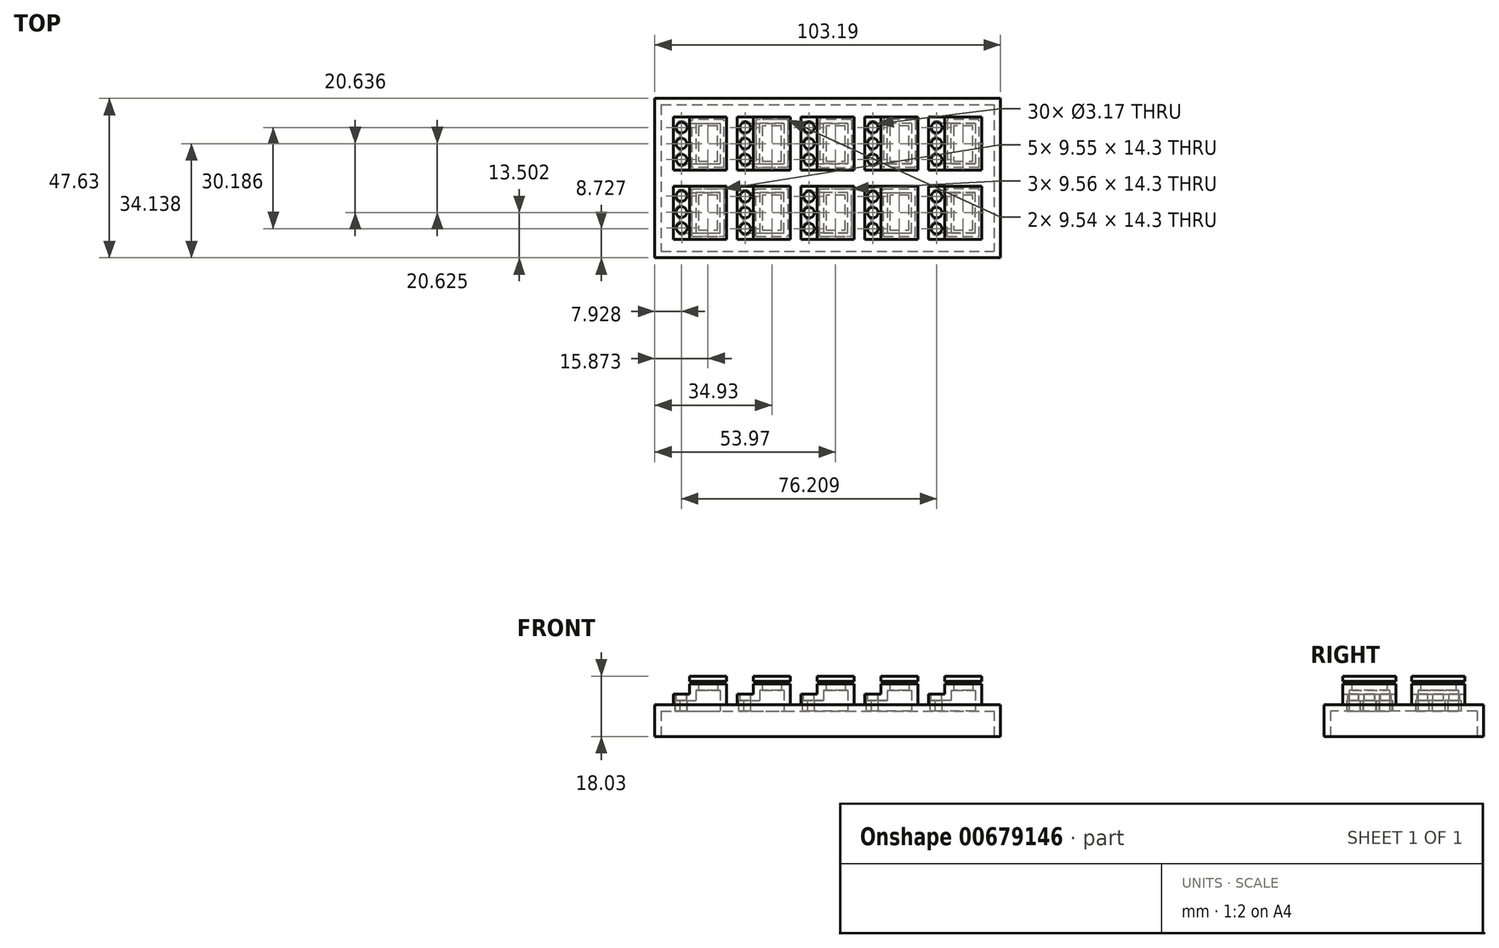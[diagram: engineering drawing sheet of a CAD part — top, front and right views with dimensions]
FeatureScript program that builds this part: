
annotation { "Feature Type Name" : "Feature", "Feature Type Description" : "" }
export const myFeature = defineFeature(function(context is Context, id is Id, definition is map)
    precondition{}
    {
        {
            var Q0;
            Q0=qCreatedBy(makeId("Top.planeOp"),FACE);
            var sketch = newSketch(context, id + "F0", { "sketchPlane" : qUnion([Q0])});
            skLineSegment(sketch, "E0.bottom", {"start": v(-47.56, -3.6) * mm, "end": v(55.63, -3.6) * mm});
            skLineSegment(sketch, "E0.top", {"start": v(-47.56, -51.22) * mm, "end": v(55.63, -51.22) * mm});
            skLineSegment(sketch, "E0.left", {"start": v(-47.56, -3.6) * mm, "end": v(-47.56, -51.22) * mm});
            skLineSegment(sketch, "E0.right", {"start": v(55.63, -3.6) * mm, "end": v(55.63, -51.22) * mm});
            skSolve(sketch);
        }
        {
            var Q0;
            Q0=makeQuery(id+"F0.imprint","IMPRINT",FACE,{"disambiguationData":[TD([[makeQuery(id+"F0.imprint","IMPRINT",EDGE,{"derivedFrom":sQuery(id+"F0.wireOp",EDGE,"E0.bottom")}),-1.0]])]});
            extrude(context, id + "F1", {"entities" : qUnion([Q0]), "depth" : 9.52 * mm, "offsetDistance" : 25.4 * mm});
        }
        {
            var Q0;
            Q0=makeQuery(id+"F1.opExtrude","CAP_FACE",FACE,{"disambiguationData":[OSD([sQuery(id+"F0.wireOp",EDGE,"E0.bottom"),sQuery(id+"F0.wireOp",EDGE,"E0.top"),sQuery(id+"F0.wireOp",EDGE,"E0.left"),sQuery(id+"F0.wireOp",EDGE,"E0.right")])],"isStart":false});
            var sketch = newSketch(context, id + "F2", { "sketchPlane" : qUnion([Q0])});
            skLineSegment(sketch, "E1.bottom", {"start": v(-42, -45.66) * mm, "end": v(-26.12, -45.66) * mm});
            skLineSegment(sketch, "E1.top", {"start": v(-42, -29.78) * mm, "end": v(-26.12, -29.78) * mm});
            skLineSegment(sketch, "E1.left", {"start": v(-42, -45.66) * mm, "end": v(-42, -29.78) * mm});
            skLineSegment(sketch, "E1.right", {"start": v(-26.12, -45.66) * mm, "end": v(-26.12, -29.78) * mm});
            skLineSegment(sketch, "E2.bottom", {"start": v(-42, -9.16) * mm, "end": v(-26.12, -9.16) * mm});
            skLineSegment(sketch, "E2.top", {"start": v(-42, -25.03) * mm, "end": v(-26.12, -25.03) * mm});
            skLineSegment(sketch, "E2.left", {"start": v(-42, -9.16) * mm, "end": v(-42, -25.03) * mm});
            skLineSegment(sketch, "E2.right", {"start": v(-26.12, -9.16) * mm, "end": v(-26.12, -25.03) * mm});
            skLineSegment(sketch, "E3.bottom", {"start": v(50.08, -45.66) * mm, "end": v(34.2, -45.66) * mm});
            skLineSegment(sketch, "E3.top", {"start": v(50.08, -29.78) * mm, "end": v(34.2, -29.78) * mm});
            skLineSegment(sketch, "E3.left", {"start": v(50.08, -45.66) * mm, "end": v(50.08, -29.78) * mm});
            skLineSegment(sketch, "E3.right", {"start": v(34.2, -45.66) * mm, "end": v(34.2, -29.78) * mm});
            skLineSegment(sketch, "E4.bottom", {"start": v(50.08, -9.16) * mm, "end": v(34.2, -9.16) * mm});
            skLineSegment(sketch, "E4.top", {"start": v(50.08, -25.03) * mm, "end": v(34.2, -25.03) * mm});
            skLineSegment(sketch, "E4.left", {"start": v(50.08, -9.16) * mm, "end": v(50.08, -25.03) * mm});
            skLineSegment(sketch, "E4.right", {"start": v(34.2, -9.16) * mm, "end": v(34.2, -25.03) * mm});
            skLineSegment(sketch, "E5.bottom", {"start": v(-22.95, -9.14) * mm, "end": v(-7.07, -9.14) * mm});
            skLineSegment(sketch, "E5.top", {"start": v(-22.95, -25.02) * mm, "end": v(-7.07, -25.02) * mm});
            skLineSegment(sketch, "E5.left", {"start": v(-22.95, -9.14) * mm, "end": v(-22.95, -25.02) * mm});
            skLineSegment(sketch, "E5.right", {"start": v(-7.07, -9.14) * mm, "end": v(-7.07, -25.02) * mm});
            skLineSegment(sketch, "E6.bottom", {"start": v(-22.95, -45.66) * mm, "end": v(-7.07, -45.66) * mm});
            skLineSegment(sketch, "E6.top", {"start": v(-22.95, -29.78) * mm, "end": v(-7.07, -29.78) * mm});
            skLineSegment(sketch, "E6.left", {"start": v(-22.95, -45.66) * mm, "end": v(-22.95, -29.78) * mm});
            skLineSegment(sketch, "E6.right", {"start": v(-7.07, -45.66) * mm, "end": v(-7.07, -29.78) * mm});
            skLineSegment(sketch, "E7.right", {"start": v(15.15, -9.14) * mm, "end": v(15.15, -25.02) * mm});
            skLineSegment(sketch, "E8.right", {"start": v(15.15, -45.66) * mm, "end": v(15.15, -29.78) * mm});
            skLineSegment(sketch, "E9.bottom", {"start": v(12.03, -45.66) * mm, "end": v(31.03, -45.66) * mm});
            skLineSegment(sketch, "E9.top", {"start": v(12.03, -29.78) * mm, "end": v(31.03, -29.78) * mm});
            skLineSegment(sketch, "E9.right", {"start": v(31.03, -45.66) * mm, "end": v(31.03, -29.78) * mm});
            skLineSegment(sketch, "E10.bottom", {"start": v(31.03, -9.14) * mm, "end": v(12.03, -9.14) * mm});
            skLineSegment(sketch, "E10.top", {"start": v(31.03, -25.02) * mm, "end": v(12.03, -25.02) * mm});
            skLineSegment(sketch, "E10.left", {"start": v(31.03, -9.14) * mm, "end": v(31.03, -25.02) * mm});
            skLineSegment(sketch, "E11.bottom", {"start": v(11.98, -45.66) * mm, "end": v(-3.9, -45.66) * mm});
            skLineSegment(sketch, "E11.top", {"start": v(11.98, -29.78) * mm, "end": v(-3.9, -29.78) * mm});
            skLineSegment(sketch, "E11.left", {"start": v(11.98, -45.66) * mm, "end": v(11.98, -29.78) * mm});
            skLineSegment(sketch, "E11.right", {"start": v(-3.9, -45.66) * mm, "end": v(-3.9, -29.78) * mm});
            skLineSegment(sketch, "E12.bottom", {"start": v(-3.9, -9.14) * mm, "end": v(11.98, -9.14) * mm});
            skLineSegment(sketch, "E12.top", {"start": v(-3.9, -25.02) * mm, "end": v(11.98, -25.02) * mm});
            skLineSegment(sketch, "E12.left", {"start": v(-3.9, -9.14) * mm, "end": v(-3.9, -25.02) * mm});
            skLineSegment(sketch, "E12.right", {"start": v(11.98, -9.14) * mm, "end": v(11.98, -25.02) * mm});
            skSolve(sketch);
        }
        {
            var Q0;
            Q0=makeQuery(id+"F2.imprint","IMPRINT",FACE,{"disambiguationData":[TD([[makeQuery(id+"F2.imprint","IMPRINT",EDGE,{"derivedFrom":sQuery(id+"F2.wireOp",EDGE,"E1.bottom")}),1.0]])]});
            var Q1;
            Q1=makeQuery(id+"F2.imprint","IMPRINT",FACE,{"disambiguationData":[TD([[makeQuery(id+"F2.imprint","IMPRINT",EDGE,{"derivedFrom":sQuery(id+"F2.wireOp",EDGE,"E2.bottom")}),-1.0]])]});
            var Q2;
            Q2=makeQuery(id+"F2.imprint","IMPRINT",FACE,{"disambiguationData":[TD([[makeQuery(id+"F2.imprint","IMPRINT",EDGE,{"derivedFrom":sQuery(id+"F2.wireOp",EDGE,"E5.bottom")}),-1.0]])]});
            var Q3;
            Q3=makeQuery(id+"F2.imprint","IMPRINT",FACE,{"disambiguationData":[TD([[makeQuery(id+"F2.imprint","IMPRINT",EDGE,{"derivedFrom":sQuery(id+"F2.wireOp",EDGE,"E6.bottom")}),1.0]])]});
            var Q4;
            Q4=makeQuery(id+"F2.imprint","IMPRINT",FACE,{"disambiguationData":[TD([[makeQuery(id+"F2.imprint","IMPRINT",EDGE,{"derivedFrom":sQuery(id+"F2.wireOp",EDGE,"E11.bottom")}),-1.0]])]});
            var Q5;
            Q5=makeQuery(id+"F2.imprint","IMPRINT",FACE,{"disambiguationData":[TD([[makeQuery(id+"F2.imprint","IMPRINT",EDGE,{"derivedFrom":sQuery(id+"F2.wireOp",EDGE,"E12.bottom")}),-1.0]])]});
            var Q6;
            {var subQ0=sQuery(id+"F2.wireOp",EDGE,"E7.right");Q6=makeQuery(id+"F2.imprint","IMPRINT",FACE,{"disambiguationData":[TD([[makeQuery(id+"F2.imprint","IMPRINT",EDGE,{"derivedFrom":subQ0}),1.0]])]});}
            var Q7;
            {var subQ0=sQuery(id+"F2.wireOp",EDGE,"E8.right");Q7=makeQuery(id+"F2.imprint","IMPRINT",FACE,{"disambiguationData":[TD([[makeQuery(id+"F2.imprint","IMPRINT",EDGE,{"derivedFrom":subQ0}),-1.0]])]});}
            var Q8;
            Q8=makeQuery(id+"F2.imprint","IMPRINT",FACE,{"disambiguationData":[TD([[makeQuery(id+"F2.imprint","IMPRINT",EDGE,{"derivedFrom":sQuery(id+"F2.wireOp",EDGE,"E3.bottom")}),-1.0]])]});
            var Q9;
            Q9=makeQuery(id+"F2.imprint","IMPRINT",FACE,{"disambiguationData":[TD([[makeQuery(id+"F2.imprint","IMPRINT",EDGE,{"derivedFrom":sQuery(id+"F2.wireOp",EDGE,"E4.bottom")}),1.0]])]});
            extrude(context, id + "F3", {"entities" : qUnion([Q0, Q1, Q2, Q3, Q4, Q5, Q6, Q7, Q8, Q9]), "operationType" : NewBodyOperationType.ADD, "depth" : 3.17 * mm, "offsetDistance" : 25.4 * mm});
        }
        {
            var Q0;
            Q0=makeQuery(id+"F3.opExtrude","CAP_FACE",FACE,{"disambiguationData":[OSD([sQuery(id+"F2.wireOp",EDGE,"E3.bottom"),sQuery(id+"F2.wireOp",EDGE,"E3.top"),sQuery(id+"F2.wireOp",EDGE,"E3.left"),sQuery(id+"F2.wireOp",EDGE,"E3.right")])],"isStart":false});
            var sketch = newSketch(context, id + "F4", { "sketchPlane" : qUnion([Q0])});
            skLineSegment(sketch, "E13.bottom", {"start": v(50.08, -45.66) * mm, "end": v(38.95, -45.66) * mm});
            skLineSegment(sketch, "E13.top", {"start": v(50.08, -29.78) * mm, "end": v(38.95, -29.78) * mm});
            skLineSegment(sketch, "E13.left", {"start": v(50.08, -45.66) * mm, "end": v(50.08, -29.78) * mm});
            skLineSegment(sketch, "E13.right", {"start": v(38.95, -45.66) * mm, "end": v(38.95, -29.78) * mm});
            skSolve(sketch);
        }
        {
            var Q0;
            Q0=makeQuery(id+"F4.imprint","IMPRINT",FACE,{"disambiguationData":[TD([[makeQuery(id+"F4.imprint","IMPRINT",EDGE,{"derivedFrom":sQuery(id+"F4.wireOp",EDGE,"E13.bottom")}),-1.0]])]});
            extrude(context, id + "F5", {"entities" : qUnion([Q0]), "operationType" : NewBodyOperationType.ADD, "depth" : 5.33 * mm, "offsetDistance" : 25.4 * mm});
        }
        {
            var Q0;
            Q0=makeQuery(id+"F3.opExtrude","CAP_FACE",FACE,{"disambiguationData":[OSD([sQuery(id+"F2.wireOp",EDGE,"E4.bottom"),sQuery(id+"F2.wireOp",EDGE,"E4.top"),sQuery(id+"F2.wireOp",EDGE,"E4.left"),sQuery(id+"F2.wireOp",EDGE,"E4.right")])],"isStart":false});
            var sketch = newSketch(context, id + "F6", { "sketchPlane" : qUnion([Q0])});
            skLineSegment(sketch, "E14.bottom", {"start": v(50.08, -25.03) * mm, "end": v(38.95, -25.03) * mm});
            skLineSegment(sketch, "E14.top", {"start": v(50.08, -8.71) * mm, "end": v(38.95, -8.71) * mm});
            skLineSegment(sketch, "E14.left", {"start": v(50.08, -25.03) * mm, "end": v(50.08, -8.71) * mm});
            skLineSegment(sketch, "E14.right", {"start": v(38.95, -25.03) * mm, "end": v(38.95, -8.71) * mm});
            skSolve(sketch);
        }
        {
            var Q0;
            {var subQ0=sQuery(id+"F6.wireOp",EDGE,"E14.bottom");Q0=makeQuery(id+"F6.imprint","IMPRINT",FACE,{"disambiguationData":[TD([[makeQuery(id+"F6.imprint","IMPRINT",EDGE,{"derivedFrom":subQ0}),-1.0]])]});}
            extrude(context, id + "F7", {"entities" : qUnion([Q0]), "operationType" : NewBodyOperationType.ADD, "depth" : 5.33 * mm, "offsetDistance" : 25.4 * mm});
        }
        {
            var Q0;
            Q0=makeQuery(id+"F3.opExtrude","CAP_FACE",FACE,{"disambiguationData":[OSD([sQuery(id+"F2.wireOp",EDGE,"E8.right"),sQuery(id+"F2.wireOp",EDGE,"E9.bottom"),sQuery(id+"F2.wireOp",EDGE,"E9.top"),sQuery(id+"F2.wireOp",EDGE,"E9.right")])],"isStart":false});
            var sketch = newSketch(context, id + "F8", { "sketchPlane" : qUnion([Q0])});
            skLineSegment(sketch, "E15.bottom", {"start": v(31.03, -45.66) * mm, "end": v(19.9, -45.66) * mm});
            skLineSegment(sketch, "E15.top", {"start": v(31.03, -29.41) * mm, "end": v(19.9, -29.41) * mm});
            skLineSegment(sketch, "E15.left", {"start": v(31.03, -45.66) * mm, "end": v(31.03, -29.41) * mm});
            skLineSegment(sketch, "E15.right", {"start": v(19.9, -45.66) * mm, "end": v(19.9, -29.41) * mm});
            skSolve(sketch);
        }
        {
            var Q0;
            {var subQ0=sQuery(id+"F8.wireOp",EDGE,"E15.bottom");Q0=makeQuery(id+"F8.imprint","IMPRINT",FACE,{"disambiguationData":[TD([[makeQuery(id+"F8.imprint","IMPRINT",EDGE,{"derivedFrom":subQ0}),1.0]])]});}
            extrude(context, id + "F9", {"entities" : qUnion([Q0]), "operationType" : NewBodyOperationType.ADD, "depth" : 5.33 * mm, "offsetDistance" : 25.4 * mm});
        }
        {
            var Q0;
            Q0=makeQuery(id+"F3.opExtrude","CAP_FACE",FACE,{"disambiguationData":[OSD([sQuery(id+"F2.wireOp",EDGE,"E7.right"),sQuery(id+"F2.wireOp",EDGE,"E10.bottom"),sQuery(id+"F2.wireOp",EDGE,"E10.top"),sQuery(id+"F2.wireOp",EDGE,"E10.left")])],"isStart":false});
            var sketch = newSketch(context, id + "F10", { "sketchPlane" : qUnion([Q0])});
            skLineSegment(sketch, "E16.bottom", {"start": v(31.03, -25.02) * mm, "end": v(19.9, -25.02) * mm});
            skLineSegment(sketch, "E16.top", {"start": v(31.03, -9.14) * mm, "end": v(19.9, -9.14) * mm});
            skLineSegment(sketch, "E16.left", {"start": v(31.03, -25.02) * mm, "end": v(31.03, -9.14) * mm});
            skLineSegment(sketch, "E16.right", {"start": v(19.9, -25.02) * mm, "end": v(19.9, -9.14) * mm});
            skSolve(sketch);
        }
        {
            var Q0;
            Q0=makeQuery(id+"F10.imprint","IMPRINT",FACE,{"disambiguationData":[TD([[makeQuery(id+"F10.imprint","IMPRINT",EDGE,{"derivedFrom":sQuery(id+"F10.wireOp",EDGE,"E16.bottom")}),-1.0]])]});
            extrude(context, id + "F11", {"entities" : qUnion([Q0]), "operationType" : NewBodyOperationType.ADD, "depth" : 5.33 * mm, "offsetDistance" : 25.4 * mm});
        }
        {
            var Q0;
            Q0=makeQuery(id+"F3.opExtrude","CAP_FACE",FACE,{"disambiguationData":[OSD([sQuery(id+"F2.wireOp",EDGE,"E11.bottom"),sQuery(id+"F2.wireOp",EDGE,"E11.top"),sQuery(id+"F2.wireOp",EDGE,"E11.left"),sQuery(id+"F2.wireOp",EDGE,"E11.right")])],"isStart":false});
            var sketch = newSketch(context, id + "F12", { "sketchPlane" : qUnion([Q0])});
            skLineSegment(sketch, "E17.bottom", {"start": v(11.98, -45.66) * mm, "end": v(0.84, -45.66) * mm});
            skLineSegment(sketch, "E17.top", {"start": v(11.98, -29.78) * mm, "end": v(0.84, -29.78) * mm});
            skLineSegment(sketch, "E17.left", {"start": v(11.98, -45.66) * mm, "end": v(11.98, -29.78) * mm});
            skLineSegment(sketch, "E17.right", {"start": v(0.84, -45.66) * mm, "end": v(0.84, -29.78) * mm});
            skSolve(sketch);
        }
        {
            var Q0;
            Q0=makeQuery(id+"F12.imprint","IMPRINT",FACE,{"disambiguationData":[TD([[makeQuery(id+"F12.imprint","IMPRINT",EDGE,{"derivedFrom":sQuery(id+"F12.wireOp",EDGE,"E17.bottom")}),-1.0]])]});
            extrude(context, id + "F13", {"entities" : qUnion([Q0]), "operationType" : NewBodyOperationType.ADD, "depth" : 5.33 * mm, "offsetDistance" : 25.4 * mm});
        }
        {
            var Q0;
            Q0=makeQuery(id+"F3.opExtrude","CAP_FACE",FACE,{"disambiguationData":[OSD([sQuery(id+"F2.wireOp",EDGE,"E12.bottom"),sQuery(id+"F2.wireOp",EDGE,"E12.top"),sQuery(id+"F2.wireOp",EDGE,"E12.left"),sQuery(id+"F2.wireOp",EDGE,"E12.right")])],"isStart":false});
            var sketch = newSketch(context, id + "F14", { "sketchPlane" : qUnion([Q0])});
            skLineSegment(sketch, "E18.bottom", {"start": v(11.98, -25.02) * mm, "end": v(0.84, -25.02) * mm});
            skLineSegment(sketch, "E18.top", {"start": v(11.98, -9.14) * mm, "end": v(0.84, -9.14) * mm});
            skLineSegment(sketch, "E18.left", {"start": v(11.98, -25.02) * mm, "end": v(11.98, -9.14) * mm});
            skLineSegment(sketch, "E18.right", {"start": v(0.84, -25.02) * mm, "end": v(0.84, -9.14) * mm});
            skSolve(sketch);
        }
        {
            var Q0;
            Q0=makeQuery(id+"F14.imprint","IMPRINT",FACE,{"disambiguationData":[TD([[makeQuery(id+"F14.imprint","IMPRINT",EDGE,{"derivedFrom":sQuery(id+"F14.wireOp",EDGE,"E18.bottom")}),1.0]])]});
            extrude(context, id + "F15", {"entities" : qUnion([Q0]), "operationType" : NewBodyOperationType.ADD, "depth" : 5.33 * mm, "offsetDistance" : 25.4 * mm});
        }
        {
            var Q0;
            Q0=makeQuery(id+"F3.opExtrude","CAP_FACE",FACE,{"disambiguationData":[OSD([sQuery(id+"F2.wireOp",EDGE,"E6.bottom"),sQuery(id+"F2.wireOp",EDGE,"E6.top"),sQuery(id+"F2.wireOp",EDGE,"E6.left"),sQuery(id+"F2.wireOp",EDGE,"E6.right")])],"isStart":false});
            var sketch = newSketch(context, id + "F16", { "sketchPlane" : qUnion([Q0])});
            skLineSegment(sketch, "E19.bottom", {"start": v(-7.07, -45.66) * mm, "end": v(-18.19, -45.66) * mm});
            skLineSegment(sketch, "E19.top", {"start": v(-7.07, -29.78) * mm, "end": v(-18.19, -29.78) * mm});
            skLineSegment(sketch, "E19.left", {"start": v(-7.07, -45.66) * mm, "end": v(-7.07, -29.78) * mm});
            skLineSegment(sketch, "E19.right", {"start": v(-18.19, -45.66) * mm, "end": v(-18.19, -29.78) * mm});
            skSolve(sketch);
        }
        {
            var Q0;
            Q0=makeQuery(id+"F16.imprint","IMPRINT",FACE,{"disambiguationData":[TD([[makeQuery(id+"F16.imprint","IMPRINT",EDGE,{"derivedFrom":sQuery(id+"F16.wireOp",EDGE,"E19.bottom")}),1.0]])]});
            extrude(context, id + "F17", {"entities" : qUnion([Q0]), "operationType" : NewBodyOperationType.ADD, "depth" : 5.33 * mm, "offsetDistance" : 25.4 * mm});
        }
        {
            var Q0;
            Q0=makeQuery(id+"F3.opExtrude","CAP_FACE",FACE,{"disambiguationData":[OSD([sQuery(id+"F2.wireOp",EDGE,"E5.bottom"),sQuery(id+"F2.wireOp",EDGE,"E5.top"),sQuery(id+"F2.wireOp",EDGE,"E5.left"),sQuery(id+"F2.wireOp",EDGE,"E5.right")])],"isStart":false});
            var sketch = newSketch(context, id + "F18", { "sketchPlane" : qUnion([Q0])});
            skLineSegment(sketch, "E20.bottom", {"start": v(-7.07, -25.02) * mm, "end": v(-18.19, -25.02) * mm});
            skLineSegment(sketch, "E20.top", {"start": v(-7.07, -9.14) * mm, "end": v(-18.19, -9.14) * mm});
            skLineSegment(sketch, "E20.left", {"start": v(-7.07, -25.02) * mm, "end": v(-7.07, -9.14) * mm});
            skLineSegment(sketch, "E20.right", {"start": v(-18.19, -25.02) * mm, "end": v(-18.19, -9.14) * mm});
            skSolve(sketch);
        }
        {
            var Q0;
            Q0=makeQuery(id+"F18.imprint","IMPRINT",FACE,{"disambiguationData":[TD([[makeQuery(id+"F18.imprint","IMPRINT",EDGE,{"derivedFrom":sQuery(id+"F18.wireOp",EDGE,"E20.bottom")}),1.0]])]});
            extrude(context, id + "F19", {"entities" : qUnion([Q0]), "operationType" : NewBodyOperationType.ADD, "depth" : 5.33 * mm, "offsetDistance" : 25.4 * mm});
        }
        {
            var Q0;
            Q0=makeQuery(id+"F3.opExtrude","CAP_FACE",FACE,{"disambiguationData":[OSD([sQuery(id+"F2.wireOp",EDGE,"E2.bottom"),sQuery(id+"F2.wireOp",EDGE,"E2.top"),sQuery(id+"F2.wireOp",EDGE,"E2.left"),sQuery(id+"F2.wireOp",EDGE,"E2.right")])],"isStart":false});
            var sketch = newSketch(context, id + "F20", { "sketchPlane" : qUnion([Q0])});
            skLineSegment(sketch, "E21.bottom", {"start": v(-26.12, -25.03) * mm, "end": v(-37.25, -25.03) * mm});
            skLineSegment(sketch, "E21.top", {"start": v(-26.12, -9.16) * mm, "end": v(-37.25, -9.16) * mm});
            skLineSegment(sketch, "E21.left", {"start": v(-26.12, -25.03) * mm, "end": v(-26.12, -9.16) * mm});
            skLineSegment(sketch, "E21.right", {"start": v(-37.25, -25.03) * mm, "end": v(-37.25, -9.16) * mm});
            skSolve(sketch);
        }
        {
            var Q0;
            Q0=makeQuery(id+"F20.imprint","IMPRINT",FACE,{"disambiguationData":[TD([[makeQuery(id+"F20.imprint","IMPRINT",EDGE,{"derivedFrom":sQuery(id+"F20.wireOp",EDGE,"E21.bottom")}),1.0]])]});
            extrude(context, id + "F21", {"entities" : qUnion([Q0]), "operationType" : NewBodyOperationType.ADD, "depth" : 5.33 * mm, "offsetDistance" : 25.4 * mm});
        }
        {
            var Q0;
            Q0=makeQuery(id+"F3.opExtrude","CAP_FACE",FACE,{"disambiguationData":[OSD([sQuery(id+"F2.wireOp",EDGE,"E1.bottom"),sQuery(id+"F2.wireOp",EDGE,"E1.top"),sQuery(id+"F2.wireOp",EDGE,"E1.left"),sQuery(id+"F2.wireOp",EDGE,"E1.right")])],"isStart":false});
            var sketch = newSketch(context, id + "F22", { "sketchPlane" : qUnion([Q0])});
            skLineSegment(sketch, "E22.bottom", {"start": v(-26.12, -45.66) * mm, "end": v(-37.25, -45.66) * mm});
            skLineSegment(sketch, "E22.top", {"start": v(-26.12, -29.78) * mm, "end": v(-37.25, -29.78) * mm});
            skLineSegment(sketch, "E22.left", {"start": v(-26.12, -45.66) * mm, "end": v(-26.12, -29.78) * mm});
            skLineSegment(sketch, "E22.right", {"start": v(-37.25, -45.66) * mm, "end": v(-37.25, -29.78) * mm});
            skSolve(sketch);
        }
        {
            var Q0;
            Q0=makeQuery(id+"F22.imprint","IMPRINT",FACE,{"disambiguationData":[TD([[makeQuery(id+"F22.imprint","IMPRINT",EDGE,{"derivedFrom":sQuery(id+"F22.wireOp",EDGE,"E22.bottom")}),1.0]])]});
            extrude(context, id + "F23", {"entities" : qUnion([Q0]), "operationType" : NewBodyOperationType.ADD, "depth" : 5.33 * mm, "offsetDistance" : 25.4 * mm});
        }
        {
            var Q0;
            Q0=makeQuery(id+"F5.boolean.opBoolean","MERGE",FACE,{"derivedFrom":[makeQuery(id+"F3.opExtrude","SWEPT_FACE",FACE,{"disambiguationData":[OSD([sQuery(id+"F2.wireOp",EDGE,"E3.bottom")])]}),makeQuery(id+"F5.opExtrude","SWEPT_FACE",FACE,{"disambiguationData":[OSD([sQuery(id+"F4.wireOp",EDGE,"E13.bottom")])]})]});
            var sketch = newSketch(context, id + "F24", { "sketchPlane" : qUnion([Q0])});
            skLineSegment(sketch, "E23.bottom", {"start": v(38.95, 16.43) * mm, "end": v(50.08, 16.43) * mm});
            skLineSegment(sketch, "E23.top", {"start": v(38.95, 15.65) * mm, "end": v(50.08, 15.65) * mm});
            skLineSegment(sketch, "E23.left", {"start": v(38.95, 16.43) * mm, "end": v(38.95, 15.65) * mm});
            skLineSegment(sketch, "E23.right", {"start": v(50.08, 16.43) * mm, "end": v(50.08, 15.65) * mm});
            skSolve(sketch);
        }
        {
            var Q0;
            Q0=makeQuery(id+"F24.imprint","IMPRINT",FACE,{"disambiguationData":[TD([[makeQuery(id+"F24.imprint","IMPRINT",EDGE,{"derivedFrom":sQuery(id+"F24.wireOp",EDGE,"E23.bottom")}),-1.0]])]});
            extrude(context, id + "F25", {"entities" : qUnion([Q0]), "operationType" : NewBodyOperationType.REMOVE, "oppositeDirection" : true, "depth" : 0.79 * mm, "offsetDistance" : 25.4 * mm});
        }
        {
            var Q0;
            Q0=makeQuery(id+"F5.boolean.opBoolean","MERGE",FACE,{"derivedFrom":[makeQuery(id+"F3.opExtrude","SWEPT_FACE",FACE,{"disambiguationData":[OSD([sQuery(id+"F2.wireOp",EDGE,"E3.left")])]}),makeQuery(id+"F5.opExtrude","SWEPT_FACE",FACE,{"disambiguationData":[OSD([sQuery(id+"F4.wireOp",EDGE,"E13.left")])]})]});
            var sketch = newSketch(context, id + "F26", { "sketchPlane" : qUnion([Q0])});
            skPoint(sketch, "E24.oppositeSnap0", {"position": v(-45.26, 15.65) * mm});
            skLineSegment(sketch, "E24.bottom", {"start": v(-45.66, 16.43) * mm, "end": v(-29.78, 16.43) * mm});
            skLineSegment(sketch, "E24.top", {"start": v(-45.66, 15.65) * mm, "end": v(-29.78, 15.65) * mm});
            skLineSegment(sketch, "E24.left", {"start": v(-45.66, 16.43) * mm, "end": v(-45.66, 15.65) * mm});
            skLineSegment(sketch, "E24.right", {"start": v(-29.78, 16.43) * mm, "end": v(-29.78, 15.65) * mm});
            skSolve(sketch);
        }
        {
            var Q0;
            {var subQ2=sQuery(id+"F26.wireOp",EDGE,"E24.right");Q0=makeQuery(id+"F26.imprint","IMPRINT",FACE,{"disambiguationData":[TD([[makeQuery(id+"F26.imprint","IMPRINT",EDGE,{"derivedFrom":subQ2}),-1.0]])]});}
            extrude(context, id + "F27", {"entities" : qUnion([Q0]), "operationType" : NewBodyOperationType.REMOVE, "oppositeDirection" : true, "depth" : 0.79 * mm, "offsetDistance" : 25.4 * mm});
        }
        {
            var Q0;
            Q0=makeQuery(id+"F5.boolean.opBoolean","MERGE",FACE,{"derivedFrom":[makeQuery(id+"F3.opExtrude","SWEPT_FACE",FACE,{"disambiguationData":[OSD([sQuery(id+"F2.wireOp",EDGE,"E3.top")])]}),makeQuery(id+"F5.opExtrude","SWEPT_FACE",FACE,{"disambiguationData":[OSD([sQuery(id+"F4.wireOp",EDGE,"E13.top")])]})]});
            var sketch = newSketch(context, id + "F28", { "sketchPlane" : qUnion([Q0])});
            skPoint(sketch, "E25.oppositeSnap0", {"position": v(-38.95, 15.37) * mm});
            skLineSegment(sketch, "E25.bottom", {"start": v(-49.3, 15.65) * mm, "end": v(-38.95, 15.65) * mm});
            skLineSegment(sketch, "E25.top", {"start": v(-49.3, 16.43) * mm, "end": v(-38.95, 16.43) * mm});
            skLineSegment(sketch, "E25.left", {"start": v(-49.3, 15.65) * mm, "end": v(-49.3, 16.43) * mm});
            skLineSegment(sketch, "E25.right", {"start": v(-38.95, 15.65) * mm, "end": v(-38.95, 16.43) * mm});
            skSolve(sketch);
        }
        {
            var Q0;
            Q0=makeQuery(id+"F28.imprint","IMPRINT",FACE,{"disambiguationData":[TD([[makeQuery(id+"F28.imprint","IMPRINT",EDGE,{"derivedFrom":sQuery(id+"F28.wireOp",EDGE,"E25.bottom")}),1.0]])]});
            extrude(context, id + "F29", {"entities" : qUnion([Q0]), "operationType" : NewBodyOperationType.REMOVE, "oppositeDirection" : true, "depth" : 0.79 * mm, "offsetDistance" : 25.4 * mm});
        }
        {
            var Q0;
            Q0=makeQuery(id+"F5.opExtrude","SWEPT_FACE",FACE,{"disambiguationData":[OSD([sQuery(id+"F4.wireOp",EDGE,"E13.right")])]});
            var sketch = newSketch(context, id + "F30", { "sketchPlane" : qUnion([Q0])});
            skLineSegment(sketch, "E26.bottom", {"start": v(44.87, 15.65) * mm, "end": v(30.57, 15.65) * mm});
            skLineSegment(sketch, "E26.top", {"start": v(44.87, 16.43) * mm, "end": v(30.57, 16.43) * mm});
            skLineSegment(sketch, "E26.left", {"start": v(44.87, 15.65) * mm, "end": v(44.87, 16.43) * mm});
            skLineSegment(sketch, "E26.right", {"start": v(30.57, 15.65) * mm, "end": v(30.57, 16.43) * mm});
            skSolve(sketch);
        }
        {
            var Q0;
            Q0 = qSketchRegion(id + "F30", true);
            extrude(context, id + "F31", {"entities" : qUnion([Q0]), "operationType" : NewBodyOperationType.REMOVE, "oppositeDirection" : true, "depth" : 0.79 * mm, "offsetDistance" : 25.4 * mm});
        }
        {
            var Q0;
            Q0=makeQuery(id+"F7.boolean.opBoolean","MERGE",FACE,{"derivedFrom":[makeQuery(id+"F3.opExtrude","SWEPT_FACE",FACE,{"disambiguationData":[OSD([sQuery(id+"F2.wireOp",EDGE,"E4.left")])]}),makeQuery(id+"F7.opExtrude","SWEPT_FACE",FACE,{"disambiguationData":[OSD([sQuery(id+"F6.wireOp",EDGE,"E14.left")])]})]});
            var sketch = newSketch(context, id + "F32", { "sketchPlane" : qUnion([Q0])});
            skLineSegment(sketch, "E27.bottom", {"start": v(-25.03, 16.43) * mm, "end": v(-9.16, 16.43) * mm});
            skLineSegment(sketch, "E27.top", {"start": v(-25.03, 15.65) * mm, "end": v(-9.16, 15.65) * mm});
            skLineSegment(sketch, "E27.left", {"start": v(-25.03, 16.43) * mm, "end": v(-25.03, 15.65) * mm});
            skLineSegment(sketch, "E27.right", {"start": v(-9.16, 16.43) * mm, "end": v(-9.16, 15.65) * mm});
            skSolve(sketch);
        }
        {
            var Q0;
            Q0=makeQuery(id+"F32.imprint","IMPRINT",FACE,{"disambiguationData":[TD([[makeQuery(id+"F32.imprint","IMPRINT",EDGE,{"derivedFrom":sQuery(id+"F32.wireOp",EDGE,"E27.bottom")}),-1.0]])]});
            extrude(context, id + "F33", {"entities" : qUnion([Q0]), "operationType" : NewBodyOperationType.REMOVE, "oppositeDirection" : true, "depth" : 0.79 * mm, "offsetDistance" : 25.4 * mm});
        }
        {
            var Q0;
            {var subQ0=sQuery(id+"F2.wireOp",EDGE,"E4.bottom");Q0=makeQuery(id+"F7.boolean.opBoolean","MERGE",FACE,{"derivedFrom":[makeQuery(id+"F3.opExtrude","SWEPT_FACE",FACE,{"disambiguationData":[OSD([subQ0])]}),makeQuery(id+"F7.opExtrude","SWEPT_FACE",FACE,{"disambiguationData":[OSD([subQ0])]})]});}
            var sketch = newSketch(context, id + "F34", { "sketchPlane" : qUnion([Q0])});
            skLineSegment(sketch, "E28.bottom", {"start": v(-49.3, 16.43) * mm, "end": v(-38.95, 16.43) * mm});
            skLineSegment(sketch, "E28.top", {"start": v(-49.3, 15.65) * mm, "end": v(-38.95, 15.65) * mm});
            skLineSegment(sketch, "E28.left", {"start": v(-49.3, 16.43) * mm, "end": v(-49.3, 15.65) * mm});
            skLineSegment(sketch, "E28.right", {"start": v(-38.95, 16.43) * mm, "end": v(-38.95, 15.65) * mm});
            skSolve(sketch);
        }
        {
            var Q0;
            Q0=makeQuery(id+"F34.imprint","IMPRINT",FACE,{"disambiguationData":[TD([[makeQuery(id+"F34.imprint","IMPRINT",EDGE,{"derivedFrom":sQuery(id+"F34.wireOp",EDGE,"E28.bottom")}),-1.0]])]});
            extrude(context, id + "F35", {"entities" : qUnion([Q0]), "operationType" : NewBodyOperationType.REMOVE, "oppositeDirection" : true, "depth" : 0.79 * mm, "offsetDistance" : 25.4 * mm});
        }
        {
            var Q0;
            Q0=makeQuery(id+"F7.boolean.opBoolean","MERGE",FACE,{"derivedFrom":[makeQuery(id+"F3.opExtrude","SWEPT_FACE",FACE,{"disambiguationData":[OSD([sQuery(id+"F2.wireOp",EDGE,"E4.top")])]}),makeQuery(id+"F7.opExtrude","SWEPT_FACE",FACE,{"disambiguationData":[OSD([sQuery(id+"F6.wireOp",EDGE,"E14.bottom")])]})]});
            var sketch = newSketch(context, id + "F36", { "sketchPlane" : qUnion([Q0])});
            skPoint(sketch, "E29.oppositeSnap0", {"position": v(49.68, 16.43) * mm});
            skLineSegment(sketch, "E29.bottom", {"start": v(49.3, 15.65) * mm, "end": v(38.95, 15.65) * mm});
            skLineSegment(sketch, "E29.top", {"start": v(49.3, 16.43) * mm, "end": v(38.95, 16.43) * mm});
            skLineSegment(sketch, "E29.left", {"start": v(49.3, 15.65) * mm, "end": v(49.3, 16.43) * mm});
            skLineSegment(sketch, "E29.right", {"start": v(38.95, 15.65) * mm, "end": v(38.95, 16.43) * mm});
            skSolve(sketch);
        }
        {
            var Q0;
            Q0=makeQuery(id+"F36.imprint","IMPRINT",FACE,{"disambiguationData":[TD([[makeQuery(id+"F36.imprint","IMPRINT",EDGE,{"derivedFrom":sQuery(id+"F36.wireOp",EDGE,"E29.bottom")}),-1.0]])]});
            extrude(context, id + "F37", {"entities" : qUnion([Q0]), "operationType" : NewBodyOperationType.REMOVE, "oppositeDirection" : true, "depth" : 0.79 * mm, "offsetDistance" : 25.4 * mm});
        }
        {
            var Q0;
            Q0=makeQuery(id+"F7.opExtrude","SWEPT_FACE",FACE,{"disambiguationData":[OSD([sQuery(id+"F6.wireOp",EDGE,"E14.right")])]});
            var sketch = newSketch(context, id + "F38", { "sketchPlane" : qUnion([Q0])});
            skLineSegment(sketch, "E30.bottom", {"start": v(9.94, 15.65) * mm, "end": v(24.24, 15.65) * mm});
            skLineSegment(sketch, "E30.top", {"start": v(9.94, 16.43) * mm, "end": v(24.24, 16.43) * mm});
            skLineSegment(sketch, "E30.left", {"start": v(9.94, 15.65) * mm, "end": v(9.94, 16.43) * mm});
            skLineSegment(sketch, "E30.right", {"start": v(24.24, 15.65) * mm, "end": v(24.24, 16.43) * mm});
            skSolve(sketch);
        }
        {
            var Q0;
            Q0=makeQuery(id+"F38.imprint","IMPRINT",FACE,{"disambiguationData":[TD([[makeQuery(id+"F38.imprint","IMPRINT",EDGE,{"derivedFrom":sQuery(id+"F38.wireOp",EDGE,"E30.bottom")}),1.0]])]});
            extrude(context, id + "F39", {"entities" : qUnion([Q0]), "operationType" : NewBodyOperationType.REMOVE, "oppositeDirection" : true, "depth" : 0.79 * mm, "offsetDistance" : 25.4 * mm});
        }
        {
            var Q0;
            Q0=makeQuery(id+"F11.boolean.opBoolean","MERGE",FACE,{"derivedFrom":[makeQuery(id+"F3.opExtrude","SWEPT_FACE",FACE,{"disambiguationData":[OSD([sQuery(id+"F2.wireOp",EDGE,"E10.bottom")])]}),makeQuery(id+"F11.opExtrude","SWEPT_FACE",FACE,{"disambiguationData":[OSD([sQuery(id+"F10.wireOp",EDGE,"E16.top")])]})]});
            var sketch = newSketch(context, id + "F40", { "sketchPlane" : qUnion([Q0])});
            skLineSegment(sketch, "E31.bottom", {"start": v(-31.03, 16.43) * mm, "end": v(-19.9, 16.43) * mm});
            skLineSegment(sketch, "E31.top", {"start": v(-31.03, 15.66) * mm, "end": v(-19.9, 15.66) * mm});
            skLineSegment(sketch, "E31.left", {"start": v(-31.03, 16.43) * mm, "end": v(-31.03, 15.66) * mm});
            skLineSegment(sketch, "E31.right", {"start": v(-19.9, 16.43) * mm, "end": v(-19.9, 15.66) * mm});
            skSolve(sketch);
        }
        {
            var Q0;
            Q0=makeQuery(id+"F40.imprint","IMPRINT",FACE,{"disambiguationData":[TD([[makeQuery(id+"F40.imprint","IMPRINT",EDGE,{"derivedFrom":sQuery(id+"F40.wireOp",EDGE,"E31.bottom")}),-1.0]])]});
            extrude(context, id + "F41", {"entities" : qUnion([Q0]), "operationType" : NewBodyOperationType.REMOVE, "oppositeDirection" : true, "depth" : 0.79 * mm, "offsetDistance" : 25.4 * mm});
        }
        {
            var Q0;
            Q0=makeQuery(id+"F11.boolean.opBoolean","MERGE",FACE,{"derivedFrom":[makeQuery(id+"F3.opExtrude","SWEPT_FACE",FACE,{"disambiguationData":[OSD([sQuery(id+"F2.wireOp",EDGE,"E10.left")])]}),makeQuery(id+"F11.opExtrude","SWEPT_FACE",FACE,{"disambiguationData":[OSD([sQuery(id+"F10.wireOp",EDGE,"E16.left")])]})]});
            var sketch = newSketch(context, id + "F42", { "sketchPlane" : qUnion([Q0])});
            skLineSegment(sketch, "E32.bottom", {"start": v(-9.93, 15.66) * mm, "end": v(-25.02, 15.66) * mm});
            skLineSegment(sketch, "E32.top", {"start": v(-9.93, 16.43) * mm, "end": v(-25.02, 16.43) * mm});
            skLineSegment(sketch, "E32.left", {"start": v(-9.93, 15.66) * mm, "end": v(-9.93, 16.43) * mm});
            skLineSegment(sketch, "E32.right", {"start": v(-25.02, 15.66) * mm, "end": v(-25.02, 16.43) * mm});
            skSolve(sketch);
        }
        {
            var Q0;
            Q0=makeQuery(id+"F42.imprint","IMPRINT",FACE,{"disambiguationData":[TD([[makeQuery(id+"F42.imprint","IMPRINT",EDGE,{"derivedFrom":sQuery(id+"F42.wireOp",EDGE,"E32.bottom")}),-1.0]])]});
            extrude(context, id + "F43", {"entities" : qUnion([Q0]), "operationType" : NewBodyOperationType.REMOVE, "oppositeDirection" : true, "depth" : 0.79 * mm, "offsetDistance" : 25.4 * mm});
        }
        {
            var Q0;
            Q0=makeQuery(id+"F11.opExtrude","SWEPT_FACE",FACE,{"disambiguationData":[OSD([sQuery(id+"F10.wireOp",EDGE,"E16.right")])]});
            var sketch = newSketch(context, id + "F44", { "sketchPlane" : qUnion([Q0])});
            skPoint(sketch, "E33.oppositeSnap0", {"position": v(25.02, 15.37) * mm});
            skLineSegment(sketch, "E33.bottom", {"start": v(9.93, 16.43) * mm, "end": v(25.02, 16.43) * mm});
            skLineSegment(sketch, "E33.top", {"start": v(9.93, 15.66) * mm, "end": v(25.02, 15.66) * mm});
            skLineSegment(sketch, "E33.left", {"start": v(9.93, 16.43) * mm, "end": v(9.93, 15.66) * mm});
            skLineSegment(sketch, "E33.right", {"start": v(25.02, 16.43) * mm, "end": v(25.02, 15.66) * mm});
            skSolve(sketch);
        }
        {
            var Q0;
            Q0=makeQuery(id+"F44.imprint","IMPRINT",FACE,{"disambiguationData":[TD([[makeQuery(id+"F44.imprint","IMPRINT",EDGE,{"derivedFrom":sQuery(id+"F44.wireOp",EDGE,"E33.bottom")}),-1.0]])]});
            extrude(context, id + "F45", {"entities" : qUnion([Q0]), "operationType" : NewBodyOperationType.REMOVE, "oppositeDirection" : true, "depth" : 0.79 * mm, "offsetDistance" : 25.4 * mm});
        }
        {
            var Q0;
            Q0=makeQuery(id+"F11.boolean.opBoolean","MERGE",FACE,{"derivedFrom":[makeQuery(id+"F3.opExtrude","SWEPT_FACE",FACE,{"disambiguationData":[OSD([sQuery(id+"F2.wireOp",EDGE,"E10.top")])]}),makeQuery(id+"F11.opExtrude","SWEPT_FACE",FACE,{"disambiguationData":[OSD([sQuery(id+"F10.wireOp",EDGE,"E16.bottom")])]})]});
            var sketch = newSketch(context, id + "F46", { "sketchPlane" : qUnion([Q0])});
            skLineSegment(sketch, "E34.bottom", {"start": v(30.24, 15.66) * mm, "end": v(20.7, 15.66) * mm});
            skLineSegment(sketch, "E34.top", {"start": v(30.24, 16.43) * mm, "end": v(20.7, 16.43) * mm});
            skLineSegment(sketch, "E34.left", {"start": v(30.24, 15.66) * mm, "end": v(30.24, 16.43) * mm});
            skLineSegment(sketch, "E34.right", {"start": v(20.7, 15.66) * mm, "end": v(20.7, 16.43) * mm});
            skSolve(sketch);
        }
        {
            var Q0;
            Q0=makeQuery(id+"F46.imprint","IMPRINT",FACE,{"disambiguationData":[TD([[makeQuery(id+"F46.imprint","IMPRINT",EDGE,{"derivedFrom":sQuery(id+"F46.wireOp",EDGE,"E34.bottom")}),-1.0]])]});
            extrude(context, id + "F47", {"entities" : qUnion([Q0]), "operationType" : NewBodyOperationType.REMOVE, "oppositeDirection" : true, "depth" : 0.79 * mm, "offsetDistance" : 25.4 * mm});
        }
        {
            var Q0;
            Q0=makeQuery(id+"F15.boolean.opBoolean","MERGE",FACE,{"derivedFrom":[makeQuery(id+"F3.opExtrude","SWEPT_FACE",FACE,{"disambiguationData":[OSD([sQuery(id+"F2.wireOp",EDGE,"E12.bottom")])]}),makeQuery(id+"F15.opExtrude","SWEPT_FACE",FACE,{"disambiguationData":[OSD([sQuery(id+"F14.wireOp",EDGE,"E18.top")])]})]});
            var sketch = newSketch(context, id + "F48", { "sketchPlane" : qUnion([Q0])});
            skLineSegment(sketch, "E35.bottom", {"start": v(-11.98, 16.43) * mm, "end": v(-0.84, 16.43) * mm});
            skLineSegment(sketch, "E35.top", {"start": v(-11.98, 15.65) * mm, "end": v(-0.84, 15.65) * mm});
            skLineSegment(sketch, "E35.left", {"start": v(-11.98, 16.43) * mm, "end": v(-11.98, 15.65) * mm});
            skLineSegment(sketch, "E35.right", {"start": v(-0.84, 16.43) * mm, "end": v(-0.84, 15.65) * mm});
            skSolve(sketch);
        }
        {
            var Q0;
            Q0=makeQuery(id+"F48.imprint","IMPRINT",FACE,{"disambiguationData":[TD([[makeQuery(id+"F48.imprint","IMPRINT",EDGE,{"derivedFrom":sQuery(id+"F48.wireOp",EDGE,"E35.bottom")}),-1.0]])]});
            extrude(context, id + "F49", {"entities" : qUnion([Q0]), "operationType" : NewBodyOperationType.REMOVE, "oppositeDirection" : true, "depth" : 0.79 * mm, "offsetDistance" : 25.4 * mm});
        }
        {
            var Q0;
            Q0=makeQuery(id+"F15.opExtrude","SWEPT_FACE",FACE,{"disambiguationData":[OSD([sQuery(id+"F14.wireOp",EDGE,"E18.right")])]});
            var sketch = newSketch(context, id + "F50", { "sketchPlane" : qUnion([Q0])});
            skLineSegment(sketch, "E36.bottom", {"start": v(9.93, 15.65) * mm, "end": v(25.02, 15.65) * mm});
            skLineSegment(sketch, "E36.top", {"start": v(9.93, 16.43) * mm, "end": v(25.02, 16.43) * mm});
            skLineSegment(sketch, "E36.left", {"start": v(9.93, 15.65) * mm, "end": v(9.93, 16.43) * mm});
            skLineSegment(sketch, "E36.right", {"start": v(25.02, 15.65) * mm, "end": v(25.02, 16.43) * mm});
            skSolve(sketch);
        }
        {
            var Q0;
            Q0=makeQuery(id+"F50.imprint","IMPRINT",FACE,{"disambiguationData":[TD([[makeQuery(id+"F50.imprint","IMPRINT",EDGE,{"derivedFrom":sQuery(id+"F50.wireOp",EDGE,"E36.bottom")}),1.0]])]});
            extrude(context, id + "F51", {"entities" : qUnion([Q0]), "operationType" : NewBodyOperationType.REMOVE, "oppositeDirection" : true, "depth" : 0.79 * mm, "offsetDistance" : 25.4 * mm});
        }
        {
            var Q0;
            Q0=makeQuery(id+"F15.boolean.opBoolean","MERGE",FACE,{"derivedFrom":[makeQuery(id+"F3.opExtrude","SWEPT_FACE",FACE,{"disambiguationData":[OSD([sQuery(id+"F2.wireOp",EDGE,"E12.top")])]}),makeQuery(id+"F15.opExtrude","SWEPT_FACE",FACE,{"disambiguationData":[OSD([sQuery(id+"F14.wireOp",EDGE,"E18.bottom")])]})]});
            var sketch = newSketch(context, id + "F52", { "sketchPlane" : qUnion([Q0])});
            skLineSegment(sketch, "E37.bottom", {"start": v(1.63, 16.43) * mm, "end": v(11.98, 16.43) * mm});
            skLineSegment(sketch, "E37.top", {"start": v(1.63, 15.65) * mm, "end": v(11.98, 15.65) * mm});
            skLineSegment(sketch, "E37.left", {"start": v(1.63, 16.43) * mm, "end": v(1.63, 15.65) * mm});
            skLineSegment(sketch, "E37.right", {"start": v(11.98, 16.43) * mm, "end": v(11.98, 15.65) * mm});
            skSolve(sketch);
        }
        {
            var Q0;
            Q0=makeQuery(id+"F52.imprint","IMPRINT",FACE,{"disambiguationData":[TD([[makeQuery(id+"F52.imprint","IMPRINT",EDGE,{"derivedFrom":sQuery(id+"F52.wireOp",EDGE,"E37.bottom")}),-1.0]])]});
            extrude(context, id + "F53", {"entities" : qUnion([Q0]), "operationType" : NewBodyOperationType.REMOVE, "oppositeDirection" : true, "depth" : 0.79 * mm, "offsetDistance" : 25.4 * mm});
        }
        {
            var Q0;
            Q0=makeQuery(id+"F15.boolean.opBoolean","MERGE",FACE,{"derivedFrom":[makeQuery(id+"F3.opExtrude","SWEPT_FACE",FACE,{"disambiguationData":[OSD([sQuery(id+"F2.wireOp",EDGE,"E12.right")])]}),makeQuery(id+"F15.opExtrude","SWEPT_FACE",FACE,{"disambiguationData":[OSD([sQuery(id+"F14.wireOp",EDGE,"E18.left")])]})]});
            var sketch = newSketch(context, id + "F54", { "sketchPlane" : qUnion([Q0])});
            skLineSegment(sketch, "E38.bottom", {"start": v(-9.93, 16.43) * mm, "end": v(-24.23, 16.43) * mm});
            skLineSegment(sketch, "E38.top", {"start": v(-9.93, 15.65) * mm, "end": v(-24.23, 15.65) * mm});
            skLineSegment(sketch, "E38.left", {"start": v(-9.93, 16.43) * mm, "end": v(-9.93, 15.65) * mm});
            skLineSegment(sketch, "E38.right", {"start": v(-24.23, 16.43) * mm, "end": v(-24.23, 15.65) * mm});
            skSolve(sketch);
        }
        {
            var Q0;
            Q0=makeQuery(id+"F54.imprint","IMPRINT",FACE,{"disambiguationData":[TD([[makeQuery(id+"F54.imprint","IMPRINT",EDGE,{"derivedFrom":sQuery(id+"F54.wireOp",EDGE,"E38.bottom")}),1.0]])]});
            extrude(context, id + "F55", {"entities" : qUnion([Q0]), "operationType" : NewBodyOperationType.REMOVE, "oppositeDirection" : true, "depth" : 0.79 * mm, "offsetDistance" : 25.4 * mm});
        }
        {
            var Q0;
            Q0=makeQuery(id+"F17.boolean.opBoolean","MERGE",FACE,{"derivedFrom":[makeQuery(id+"F3.opExtrude","SWEPT_FACE",FACE,{"disambiguationData":[OSD([sQuery(id+"F2.wireOp",EDGE,"E6.bottom")])]}),makeQuery(id+"F17.opExtrude","SWEPT_FACE",FACE,{"disambiguationData":[OSD([sQuery(id+"F16.wireOp",EDGE,"E19.bottom")])]})]});
            var sketch = newSketch(context, id + "F56", { "sketchPlane" : qUnion([Q0])});
            skLineSegment(sketch, "E39.bottom", {"start": v(-18.19, 16.43) * mm, "end": v(-7.07, 16.43) * mm});
            skLineSegment(sketch, "E39.top", {"start": v(-18.19, 15.65) * mm, "end": v(-7.07, 15.65) * mm});
            skLineSegment(sketch, "E39.left", {"start": v(-18.19, 16.43) * mm, "end": v(-18.19, 15.65) * mm});
            skLineSegment(sketch, "E39.right", {"start": v(-7.07, 16.43) * mm, "end": v(-7.07, 15.65) * mm});
            skSolve(sketch);
        }
        {
            var Q0;
            Q0=makeQuery(id+"F56.imprint","IMPRINT",FACE,{"disambiguationData":[TD([[makeQuery(id+"F56.imprint","IMPRINT",EDGE,{"derivedFrom":sQuery(id+"F56.wireOp",EDGE,"E39.bottom")}),-1.0]])]});
            extrude(context, id + "F57", {"entities" : qUnion([Q0]), "operationType" : NewBodyOperationType.REMOVE, "oppositeDirection" : true, "depth" : 0.79 * mm, "offsetDistance" : 25.4 * mm});
        }
        {
            var Q0;
            Q0=makeQuery(id+"F17.opExtrude","SWEPT_FACE",FACE,{"disambiguationData":[OSD([sQuery(id+"F16.wireOp",EDGE,"E19.right")])]});
            var sketch = newSketch(context, id + "F58", { "sketchPlane" : qUnion([Q0])});
            skLineSegment(sketch, "E40.bottom", {"start": v(44.87, 15.65) * mm, "end": v(29.78, 15.65) * mm});
            skLineSegment(sketch, "E40.top", {"start": v(44.87, 16.43) * mm, "end": v(29.78, 16.43) * mm});
            skLineSegment(sketch, "E40.left", {"start": v(44.87, 15.65) * mm, "end": v(44.87, 16.43) * mm});
            skLineSegment(sketch, "E40.right", {"start": v(29.78, 15.65) * mm, "end": v(29.78, 16.43) * mm});
            skSolve(sketch);
        }
        {
            var Q0;
            Q0=makeQuery(id+"F58.imprint","IMPRINT",FACE,{"disambiguationData":[TD([[makeQuery(id+"F58.imprint","IMPRINT",EDGE,{"derivedFrom":sQuery(id+"F58.wireOp",EDGE,"E40.bottom")}),-1.0]])]});
            extrude(context, id + "F59", {"entities" : qUnion([Q0]), "operationType" : NewBodyOperationType.REMOVE, "oppositeDirection" : true, "depth" : 0.79 * mm, "offsetDistance" : 25.4 * mm});
        }
        {
            var Q0;
            Q0=makeQuery(id+"F17.boolean.opBoolean","MERGE",FACE,{"derivedFrom":[makeQuery(id+"F3.opExtrude","SWEPT_FACE",FACE,{"disambiguationData":[OSD([sQuery(id+"F2.wireOp",EDGE,"E6.top")])]}),makeQuery(id+"F17.opExtrude","SWEPT_FACE",FACE,{"disambiguationData":[OSD([sQuery(id+"F16.wireOp",EDGE,"E19.top")])]})]});
            var sketch = newSketch(context, id + "F60", { "sketchPlane" : qUnion([Q0])});
            skLineSegment(sketch, "E41.bottom", {"start": v(17.4, 15.65) * mm, "end": v(7.07, 15.65) * mm});
            skLineSegment(sketch, "E41.top", {"start": v(17.4, 16.43) * mm, "end": v(7.07, 16.43) * mm});
            skLineSegment(sketch, "E41.left", {"start": v(17.4, 15.65) * mm, "end": v(17.4, 16.43) * mm});
            skLineSegment(sketch, "E41.right", {"start": v(7.07, 15.65) * mm, "end": v(7.07, 16.43) * mm});
            skSolve(sketch);
        }
        {
            var Q0;
            Q0=makeQuery(id+"F60.imprint","IMPRINT",FACE,{"disambiguationData":[TD([[makeQuery(id+"F60.imprint","IMPRINT",EDGE,{"derivedFrom":sQuery(id+"F60.wireOp",EDGE,"E41.bottom")}),-1.0]])]});
            extrude(context, id + "F61", {"entities" : qUnion([Q0]), "operationType" : NewBodyOperationType.REMOVE, "oppositeDirection" : true, "depth" : 0.79 * mm, "offsetDistance" : 25.4 * mm});
        }
        {
            var Q0;
            Q0=makeQuery(id+"F17.boolean.opBoolean","MERGE",FACE,{"derivedFrom":[makeQuery(id+"F3.opExtrude","SWEPT_FACE",FACE,{"disambiguationData":[OSD([sQuery(id+"F2.wireOp",EDGE,"E6.right")])]}),makeQuery(id+"F17.opExtrude","SWEPT_FACE",FACE,{"disambiguationData":[OSD([sQuery(id+"F16.wireOp",EDGE,"E19.left")])]})]});
            var sketch = newSketch(context, id + "F62", { "sketchPlane" : qUnion([Q0])});
            skLineSegment(sketch, "E42.bottom", {"start": v(-30.57, 16.43) * mm, "end": v(-44.87, 16.43) * mm});
            skLineSegment(sketch, "E42.top", {"start": v(-30.57, 15.65) * mm, "end": v(-44.87, 15.65) * mm});
            skLineSegment(sketch, "E42.left", {"start": v(-30.57, 16.43) * mm, "end": v(-30.57, 15.65) * mm});
            skLineSegment(sketch, "E42.right", {"start": v(-44.87, 16.43) * mm, "end": v(-44.87, 15.65) * mm});
            skSolve(sketch);
        }
        {
            var Q0;
            Q0=makeQuery(id+"F62.imprint","IMPRINT",FACE,{"disambiguationData":[TD([[makeQuery(id+"F62.imprint","IMPRINT",EDGE,{"derivedFrom":sQuery(id+"F62.wireOp",EDGE,"E42.bottom")}),1.0]])]});
            extrude(context, id + "F63", {"entities" : qUnion([Q0]), "operationType" : NewBodyOperationType.REMOVE, "oppositeDirection" : true, "depth" : 0.79 * mm, "offsetDistance" : 25.4 * mm});
        }
        {
            var Q0;
            Q0=makeQuery(id+"F19.boolean.opBoolean","MERGE",FACE,{"derivedFrom":[makeQuery(id+"F3.opExtrude","SWEPT_FACE",FACE,{"disambiguationData":[OSD([sQuery(id+"F2.wireOp",EDGE,"E5.bottom")])]}),makeQuery(id+"F19.opExtrude","SWEPT_FACE",FACE,{"disambiguationData":[OSD([sQuery(id+"F18.wireOp",EDGE,"E20.top")])]})]});
            var sketch = newSketch(context, id + "F64", { "sketchPlane" : qUnion([Q0])});
            skLineSegment(sketch, "E43.bottom", {"start": v(7.07, 16.43) * mm, "end": v(18.19, 16.43) * mm});
            skLineSegment(sketch, "E43.top", {"start": v(7.07, 15.65) * mm, "end": v(18.19, 15.65) * mm});
            skLineSegment(sketch, "E43.left", {"start": v(7.07, 16.43) * mm, "end": v(7.07, 15.65) * mm});
            skLineSegment(sketch, "E43.right", {"start": v(18.19, 16.43) * mm, "end": v(18.19, 15.65) * mm});
            skSolve(sketch);
        }
        {
            var Q0;
            Q0=makeQuery(id+"F64.imprint","IMPRINT",FACE,{"disambiguationData":[TD([[makeQuery(id+"F64.imprint","IMPRINT",EDGE,{"derivedFrom":sQuery(id+"F64.wireOp",EDGE,"E43.bottom")}),-1.0]])]});
            extrude(context, id + "F65", {"entities" : qUnion([Q0]), "operationType" : NewBodyOperationType.REMOVE, "oppositeDirection" : true, "depth" : 0.79 * mm, "offsetDistance" : 25.4 * mm});
        }
        {
            var Q0;
            Q0=makeQuery(id+"F19.boolean.opBoolean","MERGE",FACE,{"derivedFrom":[makeQuery(id+"F3.opExtrude","SWEPT_FACE",FACE,{"disambiguationData":[OSD([sQuery(id+"F2.wireOp",EDGE,"E5.right")])]}),makeQuery(id+"F19.opExtrude","SWEPT_FACE",FACE,{"disambiguationData":[OSD([sQuery(id+"F18.wireOp",EDGE,"E20.left")])]})]});
            var sketch = newSketch(context, id + "F66", { "sketchPlane" : qUnion([Q0])});
            skLineSegment(sketch, "E44.bottom", {"start": v(-9.93, 15.65) * mm, "end": v(-25.02, 15.65) * mm});
            skLineSegment(sketch, "E44.top", {"start": v(-9.93, 16.43) * mm, "end": v(-25.02, 16.43) * mm});
            skLineSegment(sketch, "E44.left", {"start": v(-9.93, 15.65) * mm, "end": v(-9.93, 16.43) * mm});
            skLineSegment(sketch, "E44.right", {"start": v(-25.02, 15.65) * mm, "end": v(-25.02, 16.43) * mm});
            skSolve(sketch);
        }
        {
            var Q0;
            Q0=makeQuery(id+"F66.imprint","IMPRINT",FACE,{"disambiguationData":[TD([[makeQuery(id+"F66.imprint","IMPRINT",EDGE,{"derivedFrom":sQuery(id+"F66.wireOp",EDGE,"E44.bottom")}),-1.0]])]});
            extrude(context, id + "F67", {"entities" : qUnion([Q0]), "operationType" : NewBodyOperationType.REMOVE, "oppositeDirection" : true, "depth" : 0.79 * mm, "offsetDistance" : 25.4 * mm});
        }
        {
            var Q0;
            Q0=makeQuery(id+"F19.opExtrude","SWEPT_FACE",FACE,{"disambiguationData":[OSD([sQuery(id+"F18.wireOp",EDGE,"E20.right")])]});
            var sketch = newSketch(context, id + "F68", { "sketchPlane" : qUnion([Q0])});
            skLineSegment(sketch, "E45.bottom", {"start": v(9.93, 16.43) * mm, "end": v(25.02, 16.43) * mm});
            skLineSegment(sketch, "E45.top", {"start": v(9.93, 15.65) * mm, "end": v(25.02, 15.65) * mm});
            skLineSegment(sketch, "E45.left", {"start": v(9.93, 16.43) * mm, "end": v(9.93, 15.65) * mm});
            skLineSegment(sketch, "E45.right", {"start": v(25.02, 16.43) * mm, "end": v(25.02, 15.65) * mm});
            skSolve(sketch);
        }
        {
            var Q0;
            Q0=makeQuery(id+"F68.imprint","IMPRINT",FACE,{"disambiguationData":[TD([[makeQuery(id+"F68.imprint","IMPRINT",EDGE,{"derivedFrom":sQuery(id+"F68.wireOp",EDGE,"E45.bottom")}),-1.0]])]});
            extrude(context, id + "F69", {"entities" : qUnion([Q0]), "operationType" : NewBodyOperationType.REMOVE, "oppositeDirection" : true, "depth" : 0.79 * mm, "offsetDistance" : 25.4 * mm});
        }
        {
            var Q0;
            Q0=makeQuery(id+"F19.boolean.opBoolean","MERGE",FACE,{"derivedFrom":[makeQuery(id+"F3.opExtrude","SWEPT_FACE",FACE,{"disambiguationData":[OSD([sQuery(id+"F2.wireOp",EDGE,"E5.top")])]}),makeQuery(id+"F19.opExtrude","SWEPT_FACE",FACE,{"disambiguationData":[OSD([sQuery(id+"F18.wireOp",EDGE,"E20.bottom")])]})]});
            var sketch = newSketch(context, id + "F70", { "sketchPlane" : qUnion([Q0])});
            skLineSegment(sketch, "E46.bottom", {"start": v(-7.86, 15.65) * mm, "end": v(-17.4, 15.65) * mm});
            skLineSegment(sketch, "E46.top", {"start": v(-7.86, 16.43) * mm, "end": v(-17.4, 16.43) * mm});
            skLineSegment(sketch, "E46.left", {"start": v(-7.86, 15.65) * mm, "end": v(-7.86, 16.43) * mm});
            skLineSegment(sketch, "E46.right", {"start": v(-17.4, 15.65) * mm, "end": v(-17.4, 16.43) * mm});
            skSolve(sketch);
        }
        {
            var Q0;
            Q0=makeQuery(id+"F70.imprint","IMPRINT",FACE,{"disambiguationData":[TD([[makeQuery(id+"F70.imprint","IMPRINT",EDGE,{"derivedFrom":sQuery(id+"F70.wireOp",EDGE,"E46.bottom")}),-1.0]])]});
            extrude(context, id + "F71", {"entities" : qUnion([Q0]), "operationType" : NewBodyOperationType.REMOVE, "oppositeDirection" : true, "depth" : 0.79 * mm, "offsetDistance" : 25.4 * mm});
        }
        {
            var Q0;
            Q0=makeQuery(id+"F21.boolean.opBoolean","MERGE",FACE,{"derivedFrom":[makeQuery(id+"F3.opExtrude","SWEPT_FACE",FACE,{"disambiguationData":[OSD([sQuery(id+"F2.wireOp",EDGE,"E2.right")])]}),makeQuery(id+"F21.opExtrude","SWEPT_FACE",FACE,{"disambiguationData":[OSD([sQuery(id+"F20.wireOp",EDGE,"E21.left")])]})]});
            var sketch = newSketch(context, id + "F72", { "sketchPlane" : qUnion([Q0])});
            skLineSegment(sketch, "E47.bottom", {"start": v(-25.03, 16.43) * mm, "end": v(-9.16, 16.43) * mm});
            skLineSegment(sketch, "E47.top", {"start": v(-25.03, 15.65) * mm, "end": v(-9.16, 15.65) * mm});
            skLineSegment(sketch, "E47.left", {"start": v(-25.03, 16.43) * mm, "end": v(-25.03, 15.65) * mm});
            skLineSegment(sketch, "E47.right", {"start": v(-9.16, 16.43) * mm, "end": v(-9.16, 15.65) * mm});
            skSolve(sketch);
        }
        {
            var Q0;
            Q0=makeQuery(id+"F72.imprint","IMPRINT",FACE,{"disambiguationData":[TD([[makeQuery(id+"F72.imprint","IMPRINT",EDGE,{"derivedFrom":sQuery(id+"F72.wireOp",EDGE,"E47.bottom")}),-1.0]])]});
            extrude(context, id + "F73", {"entities" : qUnion([Q0]), "operationType" : NewBodyOperationType.REMOVE, "oppositeDirection" : true, "depth" : 0.79 * mm, "offsetDistance" : 25.4 * mm});
        }
        {
            var Q0;
            Q0=makeQuery(id+"F21.boolean.opBoolean","MERGE",FACE,{"derivedFrom":[makeQuery(id+"F3.opExtrude","SWEPT_FACE",FACE,{"disambiguationData":[OSD([sQuery(id+"F2.wireOp",EDGE,"E2.top")])]}),makeQuery(id+"F21.opExtrude","SWEPT_FACE",FACE,{"disambiguationData":[OSD([sQuery(id+"F20.wireOp",EDGE,"E21.bottom")])]})]});
            var sketch = newSketch(context, id + "F74", { "sketchPlane" : qUnion([Q0])});
            skLineSegment(sketch, "E48.bottom", {"start": v(-26.9, 15.65) * mm, "end": v(-37.25, 15.65) * mm});
            skLineSegment(sketch, "E48.top", {"start": v(-26.9, 16.43) * mm, "end": v(-37.25, 16.43) * mm});
            skLineSegment(sketch, "E48.left", {"start": v(-26.9, 15.65) * mm, "end": v(-26.9, 16.43) * mm});
            skLineSegment(sketch, "E48.right", {"start": v(-37.25, 15.65) * mm, "end": v(-37.25, 16.43) * mm});
            skSolve(sketch);
        }
        {
            var Q0;
            Q0=makeQuery(id+"F74.imprint","IMPRINT",FACE,{"disambiguationData":[TD([[makeQuery(id+"F74.imprint","IMPRINT",EDGE,{"derivedFrom":sQuery(id+"F74.wireOp",EDGE,"E48.bottom")}),-1.0]])]});
            extrude(context, id + "F75", {"entities" : qUnion([Q0]), "operationType" : NewBodyOperationType.REMOVE, "oppositeDirection" : true, "depth" : 0.79 * mm, "offsetDistance" : 25.4 * mm});
        }
        {
            var Q0;
            Q0=makeQuery(id+"F21.boolean.opBoolean","MERGE",FACE,{"derivedFrom":[makeQuery(id+"F3.opExtrude","SWEPT_FACE",FACE,{"disambiguationData":[OSD([sQuery(id+"F2.wireOp",EDGE,"E2.bottom")])]}),makeQuery(id+"F21.opExtrude","SWEPT_FACE",FACE,{"disambiguationData":[OSD([sQuery(id+"F20.wireOp",EDGE,"E21.top")])]})]});
            var sketch = newSketch(context, id + "F76", { "sketchPlane" : qUnion([Q0])});
            skLineSegment(sketch, "E49.bottom", {"start": v(26.9, 15.65) * mm, "end": v(37.25, 15.65) * mm});
            skLineSegment(sketch, "E49.top", {"start": v(26.9, 16.43) * mm, "end": v(37.25, 16.43) * mm});
            skLineSegment(sketch, "E49.left", {"start": v(26.9, 15.65) * mm, "end": v(26.9, 16.43) * mm});
            skLineSegment(sketch, "E49.right", {"start": v(37.25, 15.65) * mm, "end": v(37.25, 16.43) * mm});
            skSolve(sketch);
        }
        {
            var Q0;
            Q0=makeQuery(id+"F76.imprint","IMPRINT",FACE,{"disambiguationData":[TD([[makeQuery(id+"F76.imprint","IMPRINT",EDGE,{"derivedFrom":sQuery(id+"F76.wireOp",EDGE,"E49.bottom")}),1.0]])]});
            extrude(context, id + "F77", {"entities" : qUnion([Q0]), "operationType" : NewBodyOperationType.REMOVE, "oppositeDirection" : true, "depth" : 0.79 * mm, "offsetDistance" : 25.4 * mm});
        }
        {
            var Q0;
            Q0=makeQuery(id+"F21.opExtrude","SWEPT_FACE",FACE,{"disambiguationData":[OSD([sQuery(id+"F20.wireOp",EDGE,"E21.right")])]});
            var sketch = newSketch(context, id + "F78", { "sketchPlane" : qUnion([Q0])});
            skLineSegment(sketch, "E50.bottom", {"start": v(24.24, 15.65) * mm, "end": v(9.94, 15.65) * mm});
            skLineSegment(sketch, "E50.top", {"start": v(24.24, 16.43) * mm, "end": v(9.94, 16.43) * mm});
            skLineSegment(sketch, "E50.left", {"start": v(24.24, 15.65) * mm, "end": v(24.24, 16.43) * mm});
            skLineSegment(sketch, "E50.right", {"start": v(9.94, 15.65) * mm, "end": v(9.94, 16.43) * mm});
            skSolve(sketch);
        }
        {
            var Q0;
            Q0=makeQuery(id+"F78.imprint","IMPRINT",FACE,{"disambiguationData":[TD([[makeQuery(id+"F78.imprint","IMPRINT",EDGE,{"derivedFrom":sQuery(id+"F78.wireOp",EDGE,"E50.bottom")}),-1.0]])]});
            extrude(context, id + "F79", {"entities" : qUnion([Q0]), "operationType" : NewBodyOperationType.REMOVE, "oppositeDirection" : true, "depth" : 0.79 * mm, "offsetDistance" : 25.4 * mm});
        }
        {
            var Q0;
            Q0=makeQuery(id+"F9.boolean.opBoolean","MERGE",FACE,{"derivedFrom":[makeQuery(id+"F3.opExtrude","SWEPT_FACE",FACE,{"disambiguationData":[OSD([sQuery(id+"F2.wireOp",EDGE,"E9.bottom")])]}),makeQuery(id+"F9.opExtrude","SWEPT_FACE",FACE,{"disambiguationData":[OSD([sQuery(id+"F8.wireOp",EDGE,"E15.bottom")])]})]});
            var sketch = newSketch(context, id + "F80", { "sketchPlane" : qUnion([Q0])});
            skLineSegment(sketch, "E51.bottom", {"start": v(19.9, 16.43) * mm, "end": v(31.03, 16.43) * mm});
            skLineSegment(sketch, "E51.top", {"start": v(19.9, 15.65) * mm, "end": v(31.03, 15.65) * mm});
            skLineSegment(sketch, "E51.left", {"start": v(19.9, 16.43) * mm, "end": v(19.9, 15.65) * mm});
            skLineSegment(sketch, "E51.right", {"start": v(31.03, 16.43) * mm, "end": v(31.03, 15.65) * mm});
            skSolve(sketch);
        }
        {
            var Q0;
            Q0=makeQuery(id+"F80.imprint","IMPRINT",FACE,{"disambiguationData":[TD([[makeQuery(id+"F80.imprint","IMPRINT",EDGE,{"derivedFrom":sQuery(id+"F80.wireOp",EDGE,"E51.bottom")}),-1.0]])]});
            extrude(context, id + "F81", {"entities" : qUnion([Q0]), "operationType" : NewBodyOperationType.REMOVE, "oppositeDirection" : true, "depth" : 0.79 * mm, "offsetDistance" : 25.4 * mm});
        }
        {
            var Q0;
            Q0=makeQuery(id+"F9.boolean.opBoolean","MERGE",FACE,{"derivedFrom":[makeQuery(id+"F3.opExtrude","SWEPT_FACE",FACE,{"disambiguationData":[OSD([sQuery(id+"F2.wireOp",EDGE,"E9.right")])]}),makeQuery(id+"F9.opExtrude","SWEPT_FACE",FACE,{"disambiguationData":[OSD([sQuery(id+"F8.wireOp",EDGE,"E15.left")])]})]});
            var sketch = newSketch(context, id + "F82", { "sketchPlane" : qUnion([Q0])});
            skLineSegment(sketch, "E52.bottom", {"start": v(-44.87, 16.43) * mm, "end": v(-29.78, 16.43) * mm});
            skLineSegment(sketch, "E52.top", {"start": v(-44.87, 15.65) * mm, "end": v(-29.78, 15.65) * mm});
            skLineSegment(sketch, "E52.left", {"start": v(-44.87, 16.43) * mm, "end": v(-44.87, 15.65) * mm});
            skLineSegment(sketch, "E52.right", {"start": v(-29.78, 16.43) * mm, "end": v(-29.78, 15.65) * mm});
            skSolve(sketch);
        }
        {
            var Q0;
            Q0=makeQuery(id+"F82.imprint","IMPRINT",FACE,{"disambiguationData":[TD([[makeQuery(id+"F82.imprint","IMPRINT",EDGE,{"derivedFrom":sQuery(id+"F82.wireOp",EDGE,"E52.bottom")}),-1.0]])]});
            extrude(context, id + "F83", {"entities" : qUnion([Q0]), "operationType" : NewBodyOperationType.REMOVE, "oppositeDirection" : true, "depth" : 0.79 * mm, "offsetDistance" : 25.4 * mm});
        }
        {
            var Q0;
            Q0=makeQuery(id+"F9.opExtrude","SWEPT_FACE",FACE,{"disambiguationData":[OSD([sQuery(id+"F8.wireOp",EDGE,"E15.right")])]});
            var sketch = newSketch(context, id + "F84", { "sketchPlane" : qUnion([Q0])});
            skLineSegment(sketch, "E53.bottom", {"start": v(44.87, 15.65) * mm, "end": v(29.78, 15.65) * mm});
            skLineSegment(sketch, "E53.top", {"start": v(44.87, 16.43) * mm, "end": v(29.78, 16.43) * mm});
            skLineSegment(sketch, "E53.left", {"start": v(44.87, 15.65) * mm, "end": v(44.87, 16.43) * mm});
            skLineSegment(sketch, "E53.right", {"start": v(29.78, 15.65) * mm, "end": v(29.78, 16.43) * mm});
            skSolve(sketch);
        }
        {
            var Q0;
            Q0=makeQuery(id+"F84.imprint","IMPRINT",FACE,{"disambiguationData":[TD([[makeQuery(id+"F84.imprint","IMPRINT",EDGE,{"derivedFrom":sQuery(id+"F84.wireOp",EDGE,"E53.bottom")}),-1.0]])]});
            extrude(context, id + "F85", {"entities" : qUnion([Q0]), "operationType" : NewBodyOperationType.REMOVE, "oppositeDirection" : true, "depth" : 0.79 * mm, "offsetDistance" : 25.4 * mm});
        }
        {
            var Q0;
            {var subQ0=sQuery(id+"F2.wireOp",EDGE,"E9.top");Q0=makeQuery(id+"F9.boolean.opBoolean","MERGE",FACE,{"derivedFrom":[makeQuery(id+"F3.opExtrude","SWEPT_FACE",FACE,{"disambiguationData":[OSD([subQ0])]}),makeQuery(id+"F9.opExtrude","SWEPT_FACE",FACE,{"disambiguationData":[OSD([subQ0])]})]});}
            var sketch = newSketch(context, id + "F86", { "sketchPlane" : qUnion([Q0])});
            skLineSegment(sketch, "E54.bottom", {"start": v(-20.69, 15.65) * mm, "end": v(-30.24, 15.65) * mm});
            skLineSegment(sketch, "E54.top", {"start": v(-20.69, 16.43) * mm, "end": v(-30.24, 16.43) * mm});
            skLineSegment(sketch, "E54.left", {"start": v(-20.69, 15.65) * mm, "end": v(-20.69, 16.43) * mm});
            skLineSegment(sketch, "E54.right", {"start": v(-30.24, 15.65) * mm, "end": v(-30.24, 16.43) * mm});
            skSolve(sketch);
        }
        {
            var Q0;
            Q0=makeQuery(id+"F86.imprint","IMPRINT",FACE,{"disambiguationData":[TD([[makeQuery(id+"F86.imprint","IMPRINT",EDGE,{"derivedFrom":sQuery(id+"F86.wireOp",EDGE,"E54.bottom")}),-1.0]])]});
            extrude(context, id + "F87", {"entities" : qUnion([Q0]), "operationType" : NewBodyOperationType.REMOVE, "oppositeDirection" : true, "depth" : 0.79 * mm, "offsetDistance" : 25.4 * mm});
        }
        {
            var Q0;
            Q0=makeQuery(id+"F13.boolean.opBoolean","MERGE",FACE,{"derivedFrom":[makeQuery(id+"F3.opExtrude","SWEPT_FACE",FACE,{"disambiguationData":[OSD([sQuery(id+"F2.wireOp",EDGE,"E11.bottom")])]}),makeQuery(id+"F13.opExtrude","SWEPT_FACE",FACE,{"disambiguationData":[OSD([sQuery(id+"F12.wireOp",EDGE,"E17.bottom")])]})]});
            var sketch = newSketch(context, id + "F88", { "sketchPlane" : qUnion([Q0])});
            skLineSegment(sketch, "E55.bottom", {"start": v(0.84, 16.43) * mm, "end": v(11.98, 16.43) * mm});
            skLineSegment(sketch, "E55.top", {"start": v(0.84, 15.65) * mm, "end": v(11.98, 15.65) * mm});
            skLineSegment(sketch, "E55.left", {"start": v(0.84, 16.43) * mm, "end": v(0.84, 15.65) * mm});
            skLineSegment(sketch, "E55.right", {"start": v(11.98, 16.43) * mm, "end": v(11.98, 15.65) * mm});
            skSolve(sketch);
        }
        {
            var Q0;
            Q0=makeQuery(id+"F88.imprint","IMPRINT",FACE,{"disambiguationData":[TD([[makeQuery(id+"F88.imprint","IMPRINT",EDGE,{"derivedFrom":sQuery(id+"F88.wireOp",EDGE,"E55.bottom")}),-1.0]])]});
            extrude(context, id + "F89", {"entities" : qUnion([Q0]), "operationType" : NewBodyOperationType.REMOVE, "oppositeDirection" : true, "depth" : 0.79 * mm, "offsetDistance" : 25.4 * mm});
        }
        {
            var Q0;
            Q0=makeQuery(id+"F13.opExtrude","SWEPT_FACE",FACE,{"disambiguationData":[OSD([sQuery(id+"F12.wireOp",EDGE,"E17.right")])]});
            var sketch = newSketch(context, id + "F90", { "sketchPlane" : qUnion([Q0])});
            skLineSegment(sketch, "E56.bottom", {"start": v(44.87, 16.43) * mm, "end": v(29.78, 16.43) * mm});
            skLineSegment(sketch, "E56.top", {"start": v(44.87, 15.65) * mm, "end": v(29.78, 15.65) * mm});
            skLineSegment(sketch, "E56.left", {"start": v(44.87, 16.43) * mm, "end": v(44.87, 15.65) * mm});
            skLineSegment(sketch, "E56.right", {"start": v(29.78, 16.43) * mm, "end": v(29.78, 15.65) * mm});
            skSolve(sketch);
        }
        {
            var Q0;
            Q0=makeQuery(id+"F90.imprint","IMPRINT",FACE,{"disambiguationData":[TD([[makeQuery(id+"F90.imprint","IMPRINT",EDGE,{"derivedFrom":sQuery(id+"F90.wireOp",EDGE,"E56.bottom")}),1.0]])]});
            extrude(context, id + "F91", {"entities" : qUnion([Q0]), "operationType" : NewBodyOperationType.REMOVE, "oppositeDirection" : true, "depth" : 0.79 * mm, "offsetDistance" : 25.4 * mm});
        }
        {
            var Q0;
            Q0=makeQuery(id+"F13.boolean.opBoolean","MERGE",FACE,{"derivedFrom":[makeQuery(id+"F3.opExtrude","SWEPT_FACE",FACE,{"disambiguationData":[OSD([sQuery(id+"F2.wireOp",EDGE,"E11.left")])]}),makeQuery(id+"F13.opExtrude","SWEPT_FACE",FACE,{"disambiguationData":[OSD([sQuery(id+"F12.wireOp",EDGE,"E17.left")])]})]});
            var sketch = newSketch(context, id + "F92", { "sketchPlane" : qUnion([Q0])});
            skLineSegment(sketch, "E57.bottom", {"start": v(-44.87, 15.65) * mm, "end": v(-29.78, 15.65) * mm});
            skLineSegment(sketch, "E57.top", {"start": v(-44.87, 16.43) * mm, "end": v(-29.78, 16.43) * mm});
            skLineSegment(sketch, "E57.left", {"start": v(-44.87, 15.65) * mm, "end": v(-44.87, 16.43) * mm});
            skLineSegment(sketch, "E57.right", {"start": v(-29.78, 15.65) * mm, "end": v(-29.78, 16.43) * mm});
            skSolve(sketch);
        }
        {
            var Q0;
            Q0=makeQuery(id+"F92.imprint","IMPRINT",FACE,{"disambiguationData":[TD([[makeQuery(id+"F92.imprint","IMPRINT",EDGE,{"derivedFrom":sQuery(id+"F92.wireOp",EDGE,"E57.bottom")}),1.0]])]});
            extrude(context, id + "F93", {"entities" : qUnion([Q0]), "operationType" : NewBodyOperationType.REMOVE, "oppositeDirection" : true, "depth" : 0.79 * mm, "offsetDistance" : 25.4 * mm});
        }
        {
            var Q0;
            Q0=makeQuery(id+"F13.boolean.opBoolean","MERGE",FACE,{"derivedFrom":[makeQuery(id+"F3.opExtrude","SWEPT_FACE",FACE,{"disambiguationData":[OSD([sQuery(id+"F2.wireOp",EDGE,"E11.top")])]}),makeQuery(id+"F13.opExtrude","SWEPT_FACE",FACE,{"disambiguationData":[OSD([sQuery(id+"F12.wireOp",EDGE,"E17.top")])]})]});
            var sketch = newSketch(context, id + "F94", { "sketchPlane" : qUnion([Q0])});
            skLineSegment(sketch, "E58.bottom", {"start": v(-1.63, 16.43) * mm, "end": v(-11.2, 16.43) * mm});
            skLineSegment(sketch, "E58.top", {"start": v(-1.63, 15.65) * mm, "end": v(-11.2, 15.65) * mm});
            skLineSegment(sketch, "E58.left", {"start": v(-1.63, 16.43) * mm, "end": v(-1.63, 15.65) * mm});
            skLineSegment(sketch, "E58.right", {"start": v(-11.2, 16.43) * mm, "end": v(-11.2, 15.65) * mm});
            skSolve(sketch);
        }
        {
            var Q0;
            Q0=makeQuery(id+"F94.imprint","IMPRINT",FACE,{"disambiguationData":[TD([[makeQuery(id+"F94.imprint","IMPRINT",EDGE,{"derivedFrom":sQuery(id+"F94.wireOp",EDGE,"E58.bottom")}),1.0]])]});
            extrude(context, id + "F95", {"entities" : qUnion([Q0]), "operationType" : NewBodyOperationType.REMOVE, "oppositeDirection" : true, "depth" : 0.79 * mm, "offsetDistance" : 25.4 * mm});
        }
        {
            var Q0;
            Q0=makeQuery(id+"F23.boolean.opBoolean","MERGE",FACE,{"derivedFrom":[makeQuery(id+"F3.opExtrude","SWEPT_FACE",FACE,{"disambiguationData":[OSD([sQuery(id+"F2.wireOp",EDGE,"E1.bottom")])]}),makeQuery(id+"F23.opExtrude","SWEPT_FACE",FACE,{"disambiguationData":[OSD([sQuery(id+"F22.wireOp",EDGE,"E22.bottom")])]})]});
            var sketch = newSketch(context, id + "F96", { "sketchPlane" : qUnion([Q0])});
            skLineSegment(sketch, "E59.bottom", {"start": v(-37.25, 16.43) * mm, "end": v(-26.12, 16.43) * mm});
            skLineSegment(sketch, "E59.top", {"start": v(-37.25, 15.65) * mm, "end": v(-26.12, 15.65) * mm});
            skLineSegment(sketch, "E59.left", {"start": v(-37.25, 16.43) * mm, "end": v(-37.25, 15.65) * mm});
            skLineSegment(sketch, "E59.right", {"start": v(-26.12, 16.43) * mm, "end": v(-26.12, 15.65) * mm});
            skSolve(sketch);
        }
        {
            var Q0;
            Q0=makeQuery(id+"F96.imprint","IMPRINT",FACE,{"disambiguationData":[TD([[makeQuery(id+"F96.imprint","IMPRINT",EDGE,{"derivedFrom":sQuery(id+"F96.wireOp",EDGE,"E59.bottom")}),-1.0]])]});
            extrude(context, id + "F97", {"entities" : qUnion([Q0]), "operationType" : NewBodyOperationType.REMOVE, "oppositeDirection" : true, "depth" : 0.79 * mm, "offsetDistance" : 25.4 * mm});
        }
        {
            var Q0;
            Q0=makeQuery(id+"F23.opExtrude","SWEPT_FACE",FACE,{"disambiguationData":[OSD([sQuery(id+"F22.wireOp",EDGE,"E22.right")])]});
            var sketch = newSketch(context, id + "F98", { "sketchPlane" : qUnion([Q0])});
            skLineSegment(sketch, "E60.bottom", {"start": v(44.87, 16.43) * mm, "end": v(29.78, 16.43) * mm});
            skLineSegment(sketch, "E60.top", {"start": v(44.87, 15.65) * mm, "end": v(29.78, 15.65) * mm});
            skLineSegment(sketch, "E60.left", {"start": v(44.87, 16.43) * mm, "end": v(44.87, 15.65) * mm});
            skLineSegment(sketch, "E60.right", {"start": v(29.78, 16.43) * mm, "end": v(29.78, 15.65) * mm});
            skSolve(sketch);
        }
        {
            var Q0;
            Q0=makeQuery(id+"F98.imprint","IMPRINT",FACE,{"disambiguationData":[TD([[makeQuery(id+"F98.imprint","IMPRINT",EDGE,{"derivedFrom":sQuery(id+"F98.wireOp",EDGE,"E60.bottom")}),1.0]])]});
            extrude(context, id + "F99", {"entities" : qUnion([Q0]), "operationType" : NewBodyOperationType.REMOVE, "oppositeDirection" : true, "depth" : 0.79 * mm, "offsetDistance" : 25.4 * mm});
        }
        {
            var Q0;
            Q0=makeQuery(id+"F23.boolean.opBoolean","MERGE",FACE,{"derivedFrom":[makeQuery(id+"F3.opExtrude","SWEPT_FACE",FACE,{"disambiguationData":[OSD([sQuery(id+"F2.wireOp",EDGE,"E1.top")])]}),makeQuery(id+"F23.opExtrude","SWEPT_FACE",FACE,{"disambiguationData":[OSD([sQuery(id+"F22.wireOp",EDGE,"E22.top")])]})]});
            var sketch = newSketch(context, id + "F100", { "sketchPlane" : qUnion([Q0])});
            skLineSegment(sketch, "E61.bottom", {"start": v(36.46, 16.43) * mm, "end": v(26.12, 16.43) * mm});
            skLineSegment(sketch, "E61.top", {"start": v(36.46, 15.65) * mm, "end": v(26.12, 15.65) * mm});
            skLineSegment(sketch, "E61.left", {"start": v(36.46, 16.43) * mm, "end": v(36.46, 15.65) * mm});
            skLineSegment(sketch, "E61.right", {"start": v(26.12, 16.43) * mm, "end": v(26.12, 15.65) * mm});
            skSolve(sketch);
        }
        {
            var Q0;
            Q0=makeQuery(id+"F100.imprint","IMPRINT",FACE,{"disambiguationData":[TD([[makeQuery(id+"F100.imprint","IMPRINT",EDGE,{"derivedFrom":sQuery(id+"F100.wireOp",EDGE,"E61.bottom")}),1.0]])]});
            extrude(context, id + "F101", {"entities" : qUnion([Q0]), "operationType" : NewBodyOperationType.REMOVE, "oppositeDirection" : true, "depth" : 0.79 * mm, "offsetDistance" : 25.4 * mm});
        }
        {
            var Q0;
            Q0=makeQuery(id+"F23.boolean.opBoolean","MERGE",FACE,{"derivedFrom":[makeQuery(id+"F3.opExtrude","SWEPT_FACE",FACE,{"disambiguationData":[OSD([sQuery(id+"F2.wireOp",EDGE,"E1.right")])]}),makeQuery(id+"F23.opExtrude","SWEPT_FACE",FACE,{"disambiguationData":[OSD([sQuery(id+"F22.wireOp",EDGE,"E22.left")])]})]});
            var sketch = newSketch(context, id + "F102", { "sketchPlane" : qUnion([Q0])});
            skLineSegment(sketch, "E62.bottom", {"start": v(-30.57, 16.43) * mm, "end": v(-44.87, 16.43) * mm});
            skLineSegment(sketch, "E62.top", {"start": v(-30.57, 15.65) * mm, "end": v(-44.87, 15.65) * mm});
            skLineSegment(sketch, "E62.left", {"start": v(-30.57, 16.43) * mm, "end": v(-30.57, 15.65) * mm});
            skLineSegment(sketch, "E62.right", {"start": v(-44.87, 16.43) * mm, "end": v(-44.87, 15.65) * mm});
            skSolve(sketch);
        }
        {
            var Q0;
            Q0=makeQuery(id+"F102.imprint","IMPRINT",FACE,{"disambiguationData":[TD([[makeQuery(id+"F102.imprint","IMPRINT",EDGE,{"derivedFrom":sQuery(id+"F102.wireOp",EDGE,"E62.bottom")}),1.0]])]});
            extrude(context, id + "F103", {"entities" : qUnion([Q0]), "operationType" : NewBodyOperationType.REMOVE, "oppositeDirection" : true, "depth" : 0.79 * mm, "offsetDistance" : 25.4 * mm});
        }
        {
            var Q0;
            Q0=makeQuery(id+"F1.opExtrude","CAP_FACE",FACE,{"disambiguationData":[OSD([sQuery(id+"F0.wireOp",EDGE,"E0.bottom"),sQuery(id+"F0.wireOp",EDGE,"E0.top"),sQuery(id+"F0.wireOp",EDGE,"E0.left"),sQuery(id+"F0.wireOp",EDGE,"E0.right")])],"isStart":true});
            shell(context, id + "F104", {"entities" : qUnion([Q0]), "thickness" : 1.9 * mm});
        }
        {
            var Q0;
            Q0=makeQuery(id+"F3.opExtrude","CAP_FACE",FACE,{"disambiguationData":[OSD([sQuery(id+"F2.wireOp",EDGE,"E1.bottom"),sQuery(id+"F2.wireOp",EDGE,"E1.top"),sQuery(id+"F2.wireOp",EDGE,"E1.left"),sQuery(id+"F2.wireOp",EDGE,"E1.right")])],"isStart":false});
            var sketch = newSketch(context, id + "F105", { "sketchPlane" : qUnion([Q0])});
            skCircle(sketch, "E63", {"center": v(-39.63, -37.56) * mm, "radius": 1.59 * mm});
            skCircle(sketch, "E64", {"center": v(-39.62, -32.78) * mm, "radius": 1.59 * mm});
            skCircle(sketch, "E65", {"center": v(-39.53, -42.33) * mm, "radius": 1.59 * mm});
            skSolve(sketch);
        }
        {
            var Q0;
            Q0=makeQuery(id+"F105.imprint","IMPRINT",FACE,{"disambiguationData":[TD([[makeQuery(id+"F105.imprint","IMPRINT",EDGE,{"derivedFrom":sQuery(id+"F105.wireOp",EDGE,"E64")}),1.0]])]});
            var Q1;
            Q1=makeQuery(id+"F105.imprint","IMPRINT",FACE,{"disambiguationData":[TD([[makeQuery(id+"F105.imprint","IMPRINT",EDGE,{"derivedFrom":sQuery(id+"F105.wireOp",EDGE,"E63")}),1.0]])]});
            var Q2;
            Q2=makeQuery(id+"F105.imprint","IMPRINT",FACE,{"disambiguationData":[TD([[makeQuery(id+"F105.imprint","IMPRINT",EDGE,{"derivedFrom":sQuery(id+"F105.wireOp",EDGE,"E65")}),1.0]])]});
            extrude(context, id + "F106", {"entities" : qUnion([Q0, Q1, Q2]), "operationType" : NewBodyOperationType.REMOVE, "oppositeDirection" : true, "depth" : 5.6 * mm, "offsetDistance" : 25.4 * mm});
        }
        {
            var Q0;
            Q0=makeQuery(id+"F3.opExtrude","CAP_FACE",FACE,{"disambiguationData":[OSD([sQuery(id+"F2.wireOp",EDGE,"E2.bottom"),sQuery(id+"F2.wireOp",EDGE,"E2.top"),sQuery(id+"F2.wireOp",EDGE,"E2.left"),sQuery(id+"F2.wireOp",EDGE,"E2.right")])],"isStart":false});
            var sketch = newSketch(context, id + "F107", { "sketchPlane" : qUnion([Q0])});
            skCircle(sketch, "E66", {"center": v(-39.62, -17.1) * mm, "radius": 1.59 * mm});
            skPoint(sketch, "E66.centerSnap0", {"position": v(-39.62, -9.16) * mm});
            skPoint(sketch, "E66.centerSnap1", {"position": v(-37.25, -17.1) * mm});
            skCircle(sketch, "E67", {"center": v(-39.58, -12.32) * mm, "radius": 1.59 * mm});
            skCircle(sketch, "E68", {"center": v(-39.58, -21.87) * mm, "radius": 1.59 * mm});
            skSolve(sketch);
        }
        {
            var Q0;
            Q0=makeQuery(id+"F107.imprint","IMPRINT",FACE,{"disambiguationData":[TD([[makeQuery(id+"F107.imprint","IMPRINT",EDGE,{"derivedFrom":sQuery(id+"F107.wireOp",EDGE,"E67")}),1.0]])]});
            var Q1;
            Q1=makeQuery(id+"F107.imprint","IMPRINT",FACE,{"disambiguationData":[TD([[makeQuery(id+"F107.imprint","IMPRINT",EDGE,{"derivedFrom":sQuery(id+"F107.wireOp",EDGE,"E66")}),1.0]])]});
            var Q2;
            Q2=makeQuery(id+"F107.imprint","IMPRINT",FACE,{"disambiguationData":[TD([[makeQuery(id+"F107.imprint","IMPRINT",EDGE,{"derivedFrom":sQuery(id+"F107.wireOp",EDGE,"E68")}),1.0]])]});
            extrude(context, id + "F108", {"entities" : qUnion([Q0, Q1, Q2]), "operationType" : NewBodyOperationType.REMOVE, "oppositeDirection" : true, "depth" : 5.6 * mm, "offsetDistance" : 25.4 * mm});
        }
        {
            var Q0;
            Q0=makeQuery(id+"F3.opExtrude","CAP_FACE",FACE,{"disambiguationData":[OSD([sQuery(id+"F2.wireOp",EDGE,"E6.bottom"),sQuery(id+"F2.wireOp",EDGE,"E6.top"),sQuery(id+"F2.wireOp",EDGE,"E6.left"),sQuery(id+"F2.wireOp",EDGE,"E6.right")])],"isStart":false});
            var sketch = newSketch(context, id + "F109", { "sketchPlane" : qUnion([Q0])});
            skCircle(sketch, "E69", {"center": v(-20.57, -37.72) * mm, "radius": 1.59 * mm});
            skPoint(sketch, "E69.centerSnap0", {"position": v(-20.57, -45.66) * mm});
            skPoint(sketch, "E69.centerSnap1", {"position": v(-18.19, -37.72) * mm});
            skCircle(sketch, "E70", {"center": v(-20.57, -32.94) * mm, "radius": 1.59 * mm});
            skPoint(sketch, "E70.centerSnap0", {"position": v(-20.57, -29.78) * mm});
            skCircle(sketch, "E71", {"center": v(-20.57, -42.5) * mm, "radius": 1.59 * mm});
            skSolve(sketch);
        }
        {
            var Q0;
            Q0=makeQuery(id+"F109.imprint","IMPRINT",FACE,{"disambiguationData":[TD([[makeQuery(id+"F109.imprint","IMPRINT",EDGE,{"derivedFrom":sQuery(id+"F109.wireOp",EDGE,"E70")}),1.0]])]});
            var Q1;
            Q1=makeQuery(id+"F109.imprint","IMPRINT",FACE,{"disambiguationData":[TD([[makeQuery(id+"F109.imprint","IMPRINT",EDGE,{"derivedFrom":sQuery(id+"F109.wireOp",EDGE,"E69")}),1.0]])]});
            var Q2;
            Q2=makeQuery(id+"F109.imprint","IMPRINT",FACE,{"disambiguationData":[TD([[makeQuery(id+"F109.imprint","IMPRINT",EDGE,{"derivedFrom":sQuery(id+"F109.wireOp",EDGE,"E71")}),1.0]])]});
            extrude(context, id + "F110", {"entities" : qUnion([Q0, Q1, Q2]), "operationType" : NewBodyOperationType.REMOVE, "oppositeDirection" : true, "depth" : 5.6 * mm, "offsetDistance" : 25.4 * mm});
        }
        {
            var Q0;
            Q0=makeQuery(id+"F3.opExtrude","CAP_FACE",FACE,{"disambiguationData":[OSD([sQuery(id+"F2.wireOp",EDGE,"E5.bottom"),sQuery(id+"F2.wireOp",EDGE,"E5.top"),sQuery(id+"F2.wireOp",EDGE,"E5.left"),sQuery(id+"F2.wireOp",EDGE,"E5.right")])],"isStart":false});
            var sketch = newSketch(context, id + "F111", { "sketchPlane" : qUnion([Q0])});
            skCircle(sketch, "E72", {"center": v(-20.57, -17.08) * mm, "radius": 1.59 * mm});
            skPoint(sketch, "E72.centerSnap0", {"position": v(-20.57, -25.02) * mm});
            skPoint(sketch, "E72.centerSnap1", {"position": v(-22.95, -17.08) * mm});
            skCircle(sketch, "E73", {"center": v(-20.57, -21.86) * mm, "radius": 1.59 * mm});
            skCircle(sketch, "E74", {"center": v(-20.57, -12.3) * mm, "radius": 1.59 * mm});
            skSolve(sketch);
        }
        {
            var Q0;
            Q0=makeQuery(id+"F111.imprint","IMPRINT",FACE,{"disambiguationData":[TD([[makeQuery(id+"F111.imprint","IMPRINT",EDGE,{"derivedFrom":sQuery(id+"F111.wireOp",EDGE,"E74")}),1.0]])]});
            var Q1;
            Q1=makeQuery(id+"F111.imprint","IMPRINT",FACE,{"disambiguationData":[TD([[makeQuery(id+"F111.imprint","IMPRINT",EDGE,{"derivedFrom":sQuery(id+"F111.wireOp",EDGE,"E72")}),1.0]])]});
            var Q2;
            Q2=makeQuery(id+"F111.imprint","IMPRINT",FACE,{"disambiguationData":[TD([[makeQuery(id+"F111.imprint","IMPRINT",EDGE,{"derivedFrom":sQuery(id+"F111.wireOp",EDGE,"E73")}),1.0]])]});
            extrude(context, id + "F112", {"entities" : qUnion([Q0, Q1, Q2]), "operationType" : NewBodyOperationType.REMOVE, "oppositeDirection" : true, "depth" : 5.6 * mm, "offsetDistance" : 25.4 * mm});
        }
        {
            var Q0;
            Q0=makeQuery(id+"F3.opExtrude","CAP_FACE",FACE,{"disambiguationData":[OSD([sQuery(id+"F2.wireOp",EDGE,"E12.bottom"),sQuery(id+"F2.wireOp",EDGE,"E12.top"),sQuery(id+"F2.wireOp",EDGE,"E12.left"),sQuery(id+"F2.wireOp",EDGE,"E12.right")])],"isStart":false});
            var sketch = newSketch(context, id + "F113", { "sketchPlane" : qUnion([Q0])});
            skCircle(sketch, "E75", {"center": v(-1.53, -17.08) * mm, "radius": 1.59 * mm});
            skPoint(sketch, "E75.centerSnap0", {"position": v(0.84, -17.08) * mm});
            skPoint(sketch, "E75.centerSnap1", {"position": v(-1.53, -25.02) * mm});
            skCircle(sketch, "E76", {"center": v(-1.53, -12.3) * mm, "radius": 1.59 * mm});
            skCircle(sketch, "E77", {"center": v(-1.53, -21.86) * mm, "radius": 1.59 * mm});
            skSolve(sketch);
        }
        {
            var Q0;
            Q0=makeQuery(id+"F113.imprint","IMPRINT",FACE,{"disambiguationData":[TD([[makeQuery(id+"F113.imprint","IMPRINT",EDGE,{"derivedFrom":sQuery(id+"F113.wireOp",EDGE,"E76")}),1.0]])]});
            var Q1;
            Q1=makeQuery(id+"F113.imprint","IMPRINT",FACE,{"disambiguationData":[TD([[makeQuery(id+"F113.imprint","IMPRINT",EDGE,{"derivedFrom":sQuery(id+"F113.wireOp",EDGE,"E75")}),1.0]])]});
            var Q2;
            Q2=makeQuery(id+"F113.imprint","IMPRINT",FACE,{"disambiguationData":[TD([[makeQuery(id+"F113.imprint","IMPRINT",EDGE,{"derivedFrom":sQuery(id+"F113.wireOp",EDGE,"E77")}),1.0]])]});
            extrude(context, id + "F114", {"entities" : qUnion([Q0, Q1, Q2]), "operationType" : NewBodyOperationType.REMOVE, "oppositeDirection" : true, "depth" : 5.6 * mm, "offsetDistance" : 25.4 * mm});
        }
        {
            var Q0;
            Q0=makeQuery(id+"F3.opExtrude","CAP_FACE",FACE,{"disambiguationData":[OSD([sQuery(id+"F2.wireOp",EDGE,"E11.bottom"),sQuery(id+"F2.wireOp",EDGE,"E11.top"),sQuery(id+"F2.wireOp",EDGE,"E11.left"),sQuery(id+"F2.wireOp",EDGE,"E11.right")])],"isStart":false});
            var sketch = newSketch(context, id + "F115", { "sketchPlane" : qUnion([Q0])});
            skCircle(sketch, "E78", {"center": v(-1.53, -37.72) * mm, "radius": 1.59 * mm});
            skPoint(sketch, "E78.centerSnap0", {"position": v(0.84, -37.72) * mm});
            skPoint(sketch, "E78.centerSnap1", {"position": v(-1.53, -45.66) * mm});
            skCircle(sketch, "E79", {"center": v(-1.53, -32.94) * mm, "radius": 1.59 * mm});
            skCircle(sketch, "E80", {"center": v(-1.53, -42.5) * mm, "radius": 1.59 * mm});
            skSolve(sketch);
        }
        {
            var Q0;
            Q0=makeQuery(id+"F115.imprint","IMPRINT",FACE,{"disambiguationData":[TD([[makeQuery(id+"F115.imprint","IMPRINT",EDGE,{"derivedFrom":sQuery(id+"F115.wireOp",EDGE,"E79")}),1.0]])]});
            var Q1;
            Q1=makeQuery(id+"F115.imprint","IMPRINT",FACE,{"disambiguationData":[TD([[makeQuery(id+"F115.imprint","IMPRINT",EDGE,{"derivedFrom":sQuery(id+"F115.wireOp",EDGE,"E78")}),1.0]])]});
            var Q2;
            Q2=makeQuery(id+"F115.imprint","IMPRINT",FACE,{"disambiguationData":[TD([[makeQuery(id+"F115.imprint","IMPRINT",EDGE,{"derivedFrom":sQuery(id+"F115.wireOp",EDGE,"E80")}),1.0]])]});
            extrude(context, id + "F116", {"entities" : qUnion([Q0, Q1, Q2]), "operationType" : NewBodyOperationType.REMOVE, "oppositeDirection" : true, "depth" : 5.6 * mm, "offsetDistance" : 25.4 * mm});
        }
        {
            var Q0;
            Q0=makeQuery(id+"F3.opExtrude","CAP_FACE",FACE,{"disambiguationData":[OSD([sQuery(id+"F2.wireOp",EDGE,"E8.right"),sQuery(id+"F2.wireOp",EDGE,"E9.bottom"),sQuery(id+"F2.wireOp",EDGE,"E9.top"),sQuery(id+"F2.wireOp",EDGE,"E9.right")])],"isStart":false});
            var sketch = newSketch(context, id + "F117", { "sketchPlane" : qUnion([Q0])});
            skCircle(sketch, "E81", {"center": v(17.53, -37.72) * mm, "radius": 1.59 * mm});
            skPoint(sketch, "E81.centerSnap0", {"position": v(17.53, -29.78) * mm});
            skPoint(sketch, "E81.centerSnap1", {"position": v(19.9, -37.72) * mm});
            skCircle(sketch, "E82", {"center": v(17.53, -32.94) * mm, "radius": 1.59 * mm});
            skCircle(sketch, "E83", {"center": v(17.53, -42.5) * mm, "radius": 1.59 * mm});
            skSolve(sketch);
        }
        {
            var Q0;
            Q0=makeQuery(id+"F117.imprint","IMPRINT",FACE,{"disambiguationData":[TD([[makeQuery(id+"F117.imprint","IMPRINT",EDGE,{"derivedFrom":sQuery(id+"F117.wireOp",EDGE,"E82")}),1.0]])]});
            var Q1;
            Q1=makeQuery(id+"F117.imprint","IMPRINT",FACE,{"disambiguationData":[TD([[makeQuery(id+"F117.imprint","IMPRINT",EDGE,{"derivedFrom":sQuery(id+"F117.wireOp",EDGE,"E81")}),1.0]])]});
            var Q2;
            Q2=makeQuery(id+"F117.imprint","IMPRINT",FACE,{"disambiguationData":[TD([[makeQuery(id+"F117.imprint","IMPRINT",EDGE,{"derivedFrom":sQuery(id+"F117.wireOp",EDGE,"E83")}),1.0]])]});
            extrude(context, id + "F118", {"entities" : qUnion([Q0, Q1, Q2]), "operationType" : NewBodyOperationType.REMOVE, "oppositeDirection" : true, "depth" : 5.6 * mm, "offsetDistance" : 25.4 * mm});
        }
        {
            var Q0;
            Q0=makeQuery(id+"F3.opExtrude","CAP_FACE",FACE,{"disambiguationData":[OSD([sQuery(id+"F2.wireOp",EDGE,"E7.right"),sQuery(id+"F2.wireOp",EDGE,"E10.bottom"),sQuery(id+"F2.wireOp",EDGE,"E10.top"),sQuery(id+"F2.wireOp",EDGE,"E10.left")])],"isStart":false});
            var sketch = newSketch(context, id + "F119", { "sketchPlane" : qUnion([Q0])});
            skCircle(sketch, "E84", {"center": v(17.53, -17.08) * mm, "radius": 1.59 * mm});
            skPoint(sketch, "E84.centerSnap0", {"position": v(17.53, -9.14) * mm});
            skPoint(sketch, "E84.centerSnap1", {"position": v(19.9, -17.08) * mm});
            skCircle(sketch, "E85", {"center": v(17.53, -12.3) * mm, "radius": 1.59 * mm});
            skCircle(sketch, "E86", {"center": v(17.53, -21.86) * mm, "radius": 1.59 * mm});
            skSolve(sketch);
        }
        {
            var Q0;
            Q0=makeQuery(id+"F119.imprint","IMPRINT",FACE,{"disambiguationData":[TD([[makeQuery(id+"F119.imprint","IMPRINT",EDGE,{"derivedFrom":sQuery(id+"F119.wireOp",EDGE,"E85")}),1.0]])]});
            var Q1;
            Q1=makeQuery(id+"F119.imprint","IMPRINT",FACE,{"disambiguationData":[TD([[makeQuery(id+"F119.imprint","IMPRINT",EDGE,{"derivedFrom":sQuery(id+"F119.wireOp",EDGE,"E84")}),1.0]])]});
            var Q2;
            Q2=makeQuery(id+"F119.imprint","IMPRINT",FACE,{"disambiguationData":[TD([[makeQuery(id+"F119.imprint","IMPRINT",EDGE,{"derivedFrom":sQuery(id+"F119.wireOp",EDGE,"E86")}),1.0]])]});
            extrude(context, id + "F120", {"entities" : qUnion([Q0, Q1, Q2]), "operationType" : NewBodyOperationType.REMOVE, "oppositeDirection" : true, "depth" : 5.6 * mm, "offsetDistance" : 25.4 * mm});
        }
        {
            var Q0;
            Q0=makeQuery(id+"F3.opExtrude","CAP_FACE",FACE,{"disambiguationData":[OSD([sQuery(id+"F2.wireOp",EDGE,"E4.bottom"),sQuery(id+"F2.wireOp",EDGE,"E4.top"),sQuery(id+"F2.wireOp",EDGE,"E4.left"),sQuery(id+"F2.wireOp",EDGE,"E4.right")])],"isStart":false});
            var sketch = newSketch(context, id + "F121", { "sketchPlane" : qUnion([Q0])});
            skCircle(sketch, "E87", {"center": v(36.57, -17.1) * mm, "radius": 1.59 * mm});
            skPoint(sketch, "E87.centerSnap0", {"position": v(36.57, -9.16) * mm});
            skPoint(sketch, "E87.centerSnap1", {"position": v(38.95, -17.1) * mm});
            skCircle(sketch, "E88", {"center": v(36.57, -12.32) * mm, "radius": 1.59 * mm});
            skCircle(sketch, "E89", {"center": v(36.57, -21.87) * mm, "radius": 1.59 * mm});
            skSolve(sketch);
        }
        {
            var Q0;
            Q0=makeQuery(id+"F121.imprint","IMPRINT",FACE,{"disambiguationData":[TD([[makeQuery(id+"F121.imprint","IMPRINT",EDGE,{"derivedFrom":sQuery(id+"F121.wireOp",EDGE,"E88")}),1.0]])]});
            var Q1;
            Q1=makeQuery(id+"F121.imprint","IMPRINT",FACE,{"disambiguationData":[TD([[makeQuery(id+"F121.imprint","IMPRINT",EDGE,{"derivedFrom":sQuery(id+"F121.wireOp",EDGE,"E87")}),1.0]])]});
            var Q2;
            Q2=makeQuery(id+"F121.imprint","IMPRINT",FACE,{"disambiguationData":[TD([[makeQuery(id+"F121.imprint","IMPRINT",EDGE,{"derivedFrom":sQuery(id+"F121.wireOp",EDGE,"E89")}),1.0]])]});
            extrude(context, id + "F122", {"entities" : qUnion([Q0, Q1, Q2]), "operationType" : NewBodyOperationType.REMOVE, "oppositeDirection" : true, "depth" : 5.6 * mm, "offsetDistance" : 25.4 * mm});
        }
        {
            var Q0;
            Q0=makeQuery(id+"F3.opExtrude","CAP_FACE",FACE,{"disambiguationData":[OSD([sQuery(id+"F2.wireOp",EDGE,"E3.bottom"),sQuery(id+"F2.wireOp",EDGE,"E3.top"),sQuery(id+"F2.wireOp",EDGE,"E3.left"),sQuery(id+"F2.wireOp",EDGE,"E3.right")])],"isStart":false});
            var sketch = newSketch(context, id + "F123", { "sketchPlane" : qUnion([Q0])});
            skCircle(sketch, "E90", {"center": v(36.58, -37.72) * mm, "radius": 1.59 * mm});
            skPoint(sketch, "E90.centerSnap0", {"position": v(36.58, -29.78) * mm});
            skPoint(sketch, "E90.centerSnap1", {"position": v(38.95, -37.72) * mm});
            skCircle(sketch, "E91", {"center": v(36.58, -32.94) * mm, "radius": 1.59 * mm});
            skCircle(sketch, "E92", {"center": v(36.58, -42.5) * mm, "radius": 1.59 * mm});
            skSolve(sketch);
        }
        {
            var Q0;
            Q0=makeQuery(id+"F123.imprint","IMPRINT",FACE,{"disambiguationData":[TD([[makeQuery(id+"F123.imprint","IMPRINT",EDGE,{"derivedFrom":sQuery(id+"F123.wireOp",EDGE,"E91")}),1.0]])]});
            var Q1;
            Q1=makeQuery(id+"F123.imprint","IMPRINT",FACE,{"disambiguationData":[TD([[makeQuery(id+"F123.imprint","IMPRINT",EDGE,{"derivedFrom":sQuery(id+"F123.wireOp",EDGE,"E90")}),1.0]])]});
            var Q2;
            Q2=makeQuery(id+"F123.imprint","IMPRINT",FACE,{"disambiguationData":[TD([[makeQuery(id+"F123.imprint","IMPRINT",EDGE,{"derivedFrom":sQuery(id+"F123.wireOp",EDGE,"E92")}),1.0]])]});
            extrude(context, id + "F124", {"entities" : qUnion([Q0, Q1, Q2]), "operationType" : NewBodyOperationType.REMOVE, "oppositeDirection" : true, "depth" : 5.6 * mm, "offsetDistance" : 25.4 * mm});
        }
        {
            var Q0;
            Q0=makeQuery(id+"F104.opShell","OFFSET_FACE",FACE,{"disambiguationData":[OSD([sQuery(id+"F0.wireOp",EDGE,"E0.bottom"),sQuery(id+"F0.wireOp",EDGE,"E0.top"),sQuery(id+"F0.wireOp",EDGE,"E0.left"),sQuery(id+"F0.wireOp",EDGE,"E0.right")])]});
            var sketch = newSketch(context, id + "F125", { "sketchPlane" : qUnion([Q0])});
            skCircle(sketch, "E93", {"center": v(-39.58, 12.32) * mm, "radius": 1.98 * mm});
            skCircle(sketch, "E94", {"center": v(-39.62, 17.1) * mm, "radius": 1.98 * mm});
            skCircle(sketch, "E95", {"center": v(-39.58, 21.87) * mm, "radius": 1.98 * mm});
            skCircle(sketch, "E96", {"center": v(-39.62, 32.78) * mm, "radius": 1.98 * mm});
            skCircle(sketch, "E97", {"center": v(-39.63, 37.56) * mm, "radius": 1.98 * mm});
            skCircle(sketch, "E98", {"center": v(-20.57, 12.3) * mm, "radius": 1.98 * mm});
            skCircle(sketch, "E99", {"center": v(-20.57, 17.08) * mm, "radius": 1.98 * mm});
            skCircle(sketch, "E100", {"center": v(-20.57, 21.86) * mm, "radius": 1.98 * mm});
            skCircle(sketch, "E101", {"center": v(-20.57, 32.94) * mm, "radius": 1.98 * mm});
            skCircle(sketch, "E102", {"center": v(-20.57, 42.5) * mm, "radius": 1.98 * mm});
            skCircle(sketch, "E103", {"center": v(-1.53, 12.3) * mm, "radius": 1.98 * mm});
            skCircle(sketch, "E104", {"center": v(-1.53, 21.86) * mm, "radius": 1.98 * mm});
            skCircle(sketch, "E105", {"center": v(-1.53, 32.94) * mm, "radius": 1.98 * mm});
            skCircle(sketch, "E106", {"center": v(-1.53, 37.72) * mm, "radius": 1.98 * mm});
            skCircle(sketch, "E107", {"center": v(-1.53, 42.5) * mm, "radius": 1.98 * mm});
            skCircle(sketch, "E108", {"center": v(17.53, 12.3) * mm, "radius": 1.98 * mm});
            skCircle(sketch, "E109", {"center": v(17.53, 17.08) * mm, "radius": 1.98 * mm});
            skCircle(sketch, "E110", {"center": v(17.53, 21.86) * mm, "radius": 1.98 * mm});
            skCircle(sketch, "E111", {"center": v(17.53, 32.94) * mm, "radius": 1.98 * mm});
            skCircle(sketch, "E112", {"center": v(17.53, 37.72) * mm, "radius": 1.98 * mm});
            skCircle(sketch, "E113", {"center": v(17.53, 42.5) * mm, "radius": 1.98 * mm});
            skCircle(sketch, "E114", {"center": v(36.57, 12.32) * mm, "radius": 1.98 * mm});
            skCircle(sketch, "E115", {"center": v(36.57, 17.1) * mm, "radius": 1.98 * mm});
            skCircle(sketch, "E116", {"center": v(36.57, 21.87) * mm, "radius": 1.98 * mm});
            skCircle(sketch, "E117", {"center": v(36.58, 32.94) * mm, "radius": 1.98 * mm});
            skCircle(sketch, "E118", {"center": v(36.58, 37.72) * mm, "radius": 1.98 * mm});
            skCircle(sketch, "E119", {"center": v(36.58, 42.5) * mm, "radius": 1.98 * mm});
            skCircle(sketch, "E120", {"center": v(-1.53, 17.08) * mm, "radius": 1.98 * mm});
            skCircle(sketch, "E121", {"center": v(-20.57, 37.72) * mm, "radius": 1.98 * mm});
            skCircle(sketch, "E122", {"center": v(-39.53, 42.33) * mm, "radius": 1.98 * mm});
            skSolve(sketch);
        }
        {
            var Q0;
            {var subQ5=makeQuery(id+"F108.opExtrude","SWEPT_FACE",FACE,{"disambiguationData":[OSD([sQuery(id+"F107.wireOp",EDGE,"E67")])]});var subQ6=makeQuery(id+"F104.opShell","OFFSET_FACE",FACE,{"disambiguationData":[OSD([sQuery(id+"F0.wireOp",EDGE,"E0.bottom"),sQuery(id+"F0.wireOp",EDGE,"E0.top"),sQuery(id+"F0.wireOp",EDGE,"E0.left"),sQuery(id+"F0.wireOp",EDGE,"E0.right")])]});var subQ9=makeQuery(id+"F108.boolean.opBoolean","INTERSECT",EDGE,{"derivedFrom":[subQ6,subQ5]});Q0=makeQuery(id+"F125.imprint","IMPRINT",FACE,{"disambiguationData":[TD([[makeQuery(id+"F125.imprint","IMPRINT",EDGE,{"derivedFrom":subQ9}),1.0]])]});}
            var Q1;
            {var subQ3=makeQuery(id+"F104.opShell","OFFSET_FACE",FACE,{"disambiguationData":[OSD([sQuery(id+"F0.wireOp",EDGE,"E0.bottom"),sQuery(id+"F0.wireOp",EDGE,"E0.top"),sQuery(id+"F0.wireOp",EDGE,"E0.left"),sQuery(id+"F0.wireOp",EDGE,"E0.right")])]});var subQ4=makeQuery(id+"F108.opExtrude","SWEPT_FACE",FACE,{"disambiguationData":[OSD([sQuery(id+"F107.wireOp",EDGE,"E66")])]});var subQ10=makeQuery(id+"F108.boolean.opBoolean","INTERSECT",EDGE,{"derivedFrom":[subQ3,subQ4]});Q1=makeQuery(id+"F125.imprint","IMPRINT",FACE,{"disambiguationData":[TD([[makeQuery(id+"F125.imprint","IMPRINT",EDGE,{"derivedFrom":subQ10}),1.0]])]});}
            var Q2;
            {var subQ5=makeQuery(id+"F104.opShell","OFFSET_FACE",FACE,{"disambiguationData":[OSD([sQuery(id+"F0.wireOp",EDGE,"E0.bottom"),sQuery(id+"F0.wireOp",EDGE,"E0.top"),sQuery(id+"F0.wireOp",EDGE,"E0.left"),sQuery(id+"F0.wireOp",EDGE,"E0.right")])]});var subQ6=makeQuery(id+"F108.opExtrude","SWEPT_FACE",FACE,{"disambiguationData":[OSD([sQuery(id+"F107.wireOp",EDGE,"E68")])]});var subQ9=makeQuery(id+"F108.boolean.opBoolean","INTERSECT",EDGE,{"derivedFrom":[subQ5,subQ6]});Q2=makeQuery(id+"F125.imprint","IMPRINT",FACE,{"disambiguationData":[TD([[makeQuery(id+"F125.imprint","IMPRINT",EDGE,{"derivedFrom":subQ9}),1.0]])]});}
            var Q3;
            {var subQ5=makeQuery(id+"F104.opShell","OFFSET_FACE",FACE,{"disambiguationData":[OSD([sQuery(id+"F0.wireOp",EDGE,"E0.bottom"),sQuery(id+"F0.wireOp",EDGE,"E0.top"),sQuery(id+"F0.wireOp",EDGE,"E0.left"),sQuery(id+"F0.wireOp",EDGE,"E0.right")])]});var subQ6=makeQuery(id+"F106.opExtrude","SWEPT_FACE",FACE,{"disambiguationData":[OSD([sQuery(id+"F105.wireOp",EDGE,"E64")])]});var subQ9=makeQuery(id+"F106.boolean.opBoolean","INTERSECT",EDGE,{"derivedFrom":[subQ5,subQ6]});Q3=makeQuery(id+"F125.imprint","IMPRINT",FACE,{"disambiguationData":[TD([[makeQuery(id+"F125.imprint","IMPRINT",EDGE,{"derivedFrom":subQ9}),1.0]])]});}
            var Q4;
            {var subQ3=makeQuery(id+"F104.opShell","OFFSET_FACE",FACE,{"disambiguationData":[OSD([sQuery(id+"F0.wireOp",EDGE,"E0.bottom"),sQuery(id+"F0.wireOp",EDGE,"E0.top"),sQuery(id+"F0.wireOp",EDGE,"E0.left"),sQuery(id+"F0.wireOp",EDGE,"E0.right")])]});var subQ4=makeQuery(id+"F106.opExtrude","SWEPT_FACE",FACE,{"disambiguationData":[OSD([sQuery(id+"F105.wireOp",EDGE,"E63")])]});var subQ10=makeQuery(id+"F106.boolean.opBoolean","INTERSECT",EDGE,{"derivedFrom":[subQ3,subQ4]});Q4=makeQuery(id+"F125.imprint","IMPRINT",FACE,{"disambiguationData":[TD([[makeQuery(id+"F125.imprint","IMPRINT",EDGE,{"derivedFrom":subQ10}),1.0]])]});}
            var Q5;
            {var subQ5=makeQuery(id+"F104.opShell","OFFSET_FACE",FACE,{"disambiguationData":[OSD([sQuery(id+"F0.wireOp",EDGE,"E0.bottom"),sQuery(id+"F0.wireOp",EDGE,"E0.top"),sQuery(id+"F0.wireOp",EDGE,"E0.left"),sQuery(id+"F0.wireOp",EDGE,"E0.right")])]});var subQ6=makeQuery(id+"F106.opExtrude","SWEPT_FACE",FACE,{"disambiguationData":[OSD([sQuery(id+"F105.wireOp",EDGE,"E65")])]});var subQ9=makeQuery(id+"F106.boolean.opBoolean","INTERSECT",EDGE,{"derivedFrom":[subQ5,subQ6]});Q5=makeQuery(id+"F125.imprint","IMPRINT",FACE,{"disambiguationData":[TD([[makeQuery(id+"F125.imprint","IMPRINT",EDGE,{"derivedFrom":subQ9}),1.0]])]});}
            var Q6;
            {var subQ5=makeQuery(id+"F104.opShell","OFFSET_FACE",FACE,{"disambiguationData":[OSD([sQuery(id+"F0.wireOp",EDGE,"E0.bottom"),sQuery(id+"F0.wireOp",EDGE,"E0.top"),sQuery(id+"F0.wireOp",EDGE,"E0.left"),sQuery(id+"F0.wireOp",EDGE,"E0.right")])]});var subQ6=makeQuery(id+"F112.opExtrude","SWEPT_FACE",FACE,{"disambiguationData":[OSD([sQuery(id+"F111.wireOp",EDGE,"E74")])]});var subQ9=makeQuery(id+"F112.boolean.opBoolean","INTERSECT",EDGE,{"derivedFrom":[subQ5,subQ6]});Q6=makeQuery(id+"F125.imprint","IMPRINT",FACE,{"disambiguationData":[TD([[makeQuery(id+"F125.imprint","IMPRINT",EDGE,{"derivedFrom":subQ9}),1.0]])]});}
            var Q7;
            {var subQ3=makeQuery(id+"F104.opShell","OFFSET_FACE",FACE,{"disambiguationData":[OSD([sQuery(id+"F0.wireOp",EDGE,"E0.bottom"),sQuery(id+"F0.wireOp",EDGE,"E0.top"),sQuery(id+"F0.wireOp",EDGE,"E0.left"),sQuery(id+"F0.wireOp",EDGE,"E0.right")])]});var subQ4=makeQuery(id+"F112.opExtrude","SWEPT_FACE",FACE,{"disambiguationData":[OSD([sQuery(id+"F111.wireOp",EDGE,"E72")])]});var subQ10=makeQuery(id+"F112.boolean.opBoolean","INTERSECT",EDGE,{"derivedFrom":[subQ3,subQ4]});Q7=makeQuery(id+"F125.imprint","IMPRINT",FACE,{"disambiguationData":[TD([[makeQuery(id+"F125.imprint","IMPRINT",EDGE,{"derivedFrom":subQ10}),1.0]])]});}
            var Q8;
            {var subQ5=makeQuery(id+"F112.opExtrude","SWEPT_FACE",FACE,{"disambiguationData":[OSD([sQuery(id+"F111.wireOp",EDGE,"E73")])]});var subQ6=makeQuery(id+"F104.opShell","OFFSET_FACE",FACE,{"disambiguationData":[OSD([sQuery(id+"F0.wireOp",EDGE,"E0.bottom"),sQuery(id+"F0.wireOp",EDGE,"E0.top"),sQuery(id+"F0.wireOp",EDGE,"E0.left"),sQuery(id+"F0.wireOp",EDGE,"E0.right")])]});var subQ9=makeQuery(id+"F112.boolean.opBoolean","INTERSECT",EDGE,{"derivedFrom":[subQ6,subQ5]});Q8=makeQuery(id+"F125.imprint","IMPRINT",FACE,{"disambiguationData":[TD([[makeQuery(id+"F125.imprint","IMPRINT",EDGE,{"derivedFrom":subQ9}),1.0]])]});}
            var Q9;
            {var subQ5=makeQuery(id+"F104.opShell","OFFSET_FACE",FACE,{"disambiguationData":[OSD([sQuery(id+"F0.wireOp",EDGE,"E0.bottom"),sQuery(id+"F0.wireOp",EDGE,"E0.top"),sQuery(id+"F0.wireOp",EDGE,"E0.left"),sQuery(id+"F0.wireOp",EDGE,"E0.right")])]});var subQ6=makeQuery(id+"F110.opExtrude","SWEPT_FACE",FACE,{"disambiguationData":[OSD([sQuery(id+"F109.wireOp",EDGE,"E70")])]});var subQ9=makeQuery(id+"F110.boolean.opBoolean","INTERSECT",EDGE,{"derivedFrom":[subQ5,subQ6]});Q9=makeQuery(id+"F125.imprint","IMPRINT",FACE,{"disambiguationData":[TD([[makeQuery(id+"F125.imprint","IMPRINT",EDGE,{"derivedFrom":subQ9}),1.0]])]});}
            var Q10;
            {var subQ3=makeQuery(id+"F104.opShell","OFFSET_FACE",FACE,{"disambiguationData":[OSD([sQuery(id+"F0.wireOp",EDGE,"E0.bottom"),sQuery(id+"F0.wireOp",EDGE,"E0.top"),sQuery(id+"F0.wireOp",EDGE,"E0.left"),sQuery(id+"F0.wireOp",EDGE,"E0.right")])]});var subQ4=makeQuery(id+"F110.opExtrude","SWEPT_FACE",FACE,{"disambiguationData":[OSD([sQuery(id+"F109.wireOp",EDGE,"E69")])]});var subQ10=makeQuery(id+"F110.boolean.opBoolean","INTERSECT",EDGE,{"derivedFrom":[subQ3,subQ4]});Q10=makeQuery(id+"F125.imprint","IMPRINT",FACE,{"disambiguationData":[TD([[makeQuery(id+"F125.imprint","IMPRINT",EDGE,{"derivedFrom":subQ10}),1.0]])]});}
            var Q11;
            {var subQ5=makeQuery(id+"F104.opShell","OFFSET_FACE",FACE,{"disambiguationData":[OSD([sQuery(id+"F0.wireOp",EDGE,"E0.bottom"),sQuery(id+"F0.wireOp",EDGE,"E0.top"),sQuery(id+"F0.wireOp",EDGE,"E0.left"),sQuery(id+"F0.wireOp",EDGE,"E0.right")])]});var subQ6=makeQuery(id+"F110.opExtrude","SWEPT_FACE",FACE,{"disambiguationData":[OSD([sQuery(id+"F109.wireOp",EDGE,"E71")])]});var subQ9=makeQuery(id+"F110.boolean.opBoolean","INTERSECT",EDGE,{"derivedFrom":[subQ5,subQ6]});Q11=makeQuery(id+"F125.imprint","IMPRINT",FACE,{"disambiguationData":[TD([[makeQuery(id+"F125.imprint","IMPRINT",EDGE,{"derivedFrom":subQ9}),1.0]])]});}
            var Q12;
            {var subQ5=makeQuery(id+"F104.opShell","OFFSET_FACE",FACE,{"disambiguationData":[OSD([sQuery(id+"F0.wireOp",EDGE,"E0.bottom"),sQuery(id+"F0.wireOp",EDGE,"E0.top"),sQuery(id+"F0.wireOp",EDGE,"E0.left"),sQuery(id+"F0.wireOp",EDGE,"E0.right")])]});var subQ6=makeQuery(id+"F114.opExtrude","SWEPT_FACE",FACE,{"disambiguationData":[OSD([sQuery(id+"F113.wireOp",EDGE,"E76")])]});var subQ9=makeQuery(id+"F114.boolean.opBoolean","INTERSECT",EDGE,{"derivedFrom":[subQ5,subQ6]});Q12=makeQuery(id+"F125.imprint","IMPRINT",FACE,{"disambiguationData":[TD([[makeQuery(id+"F125.imprint","IMPRINT",EDGE,{"derivedFrom":subQ9}),1.0]])]});}
            var Q13;
            {var subQ3=makeQuery(id+"F104.opShell","OFFSET_FACE",FACE,{"disambiguationData":[OSD([sQuery(id+"F0.wireOp",EDGE,"E0.bottom"),sQuery(id+"F0.wireOp",EDGE,"E0.top"),sQuery(id+"F0.wireOp",EDGE,"E0.left"),sQuery(id+"F0.wireOp",EDGE,"E0.right")])]});var subQ4=makeQuery(id+"F114.opExtrude","SWEPT_FACE",FACE,{"disambiguationData":[OSD([sQuery(id+"F113.wireOp",EDGE,"E75")])]});var subQ10=makeQuery(id+"F114.boolean.opBoolean","INTERSECT",EDGE,{"derivedFrom":[subQ3,subQ4]});Q13=makeQuery(id+"F125.imprint","IMPRINT",FACE,{"disambiguationData":[TD([[makeQuery(id+"F125.imprint","IMPRINT",EDGE,{"derivedFrom":subQ10}),1.0]])]});}
            var Q14;
            {var subQ5=makeQuery(id+"F104.opShell","OFFSET_FACE",FACE,{"disambiguationData":[OSD([sQuery(id+"F0.wireOp",EDGE,"E0.bottom"),sQuery(id+"F0.wireOp",EDGE,"E0.top"),sQuery(id+"F0.wireOp",EDGE,"E0.left"),sQuery(id+"F0.wireOp",EDGE,"E0.right")])]});var subQ6=makeQuery(id+"F114.opExtrude","SWEPT_FACE",FACE,{"disambiguationData":[OSD([sQuery(id+"F113.wireOp",EDGE,"E77")])]});var subQ9=makeQuery(id+"F114.boolean.opBoolean","INTERSECT",EDGE,{"derivedFrom":[subQ5,subQ6]});Q14=makeQuery(id+"F125.imprint","IMPRINT",FACE,{"disambiguationData":[TD([[makeQuery(id+"F125.imprint","IMPRINT",EDGE,{"derivedFrom":subQ9}),1.0]])]});}
            var Q15;
            {var subQ5=makeQuery(id+"F104.opShell","OFFSET_FACE",FACE,{"disambiguationData":[OSD([sQuery(id+"F0.wireOp",EDGE,"E0.bottom"),sQuery(id+"F0.wireOp",EDGE,"E0.top"),sQuery(id+"F0.wireOp",EDGE,"E0.left"),sQuery(id+"F0.wireOp",EDGE,"E0.right")])]});var subQ6=makeQuery(id+"F116.opExtrude","SWEPT_FACE",FACE,{"disambiguationData":[OSD([sQuery(id+"F115.wireOp",EDGE,"E79")])]});var subQ9=makeQuery(id+"F116.boolean.opBoolean","INTERSECT",EDGE,{"derivedFrom":[subQ5,subQ6]});Q15=makeQuery(id+"F125.imprint","IMPRINT",FACE,{"disambiguationData":[TD([[makeQuery(id+"F125.imprint","IMPRINT",EDGE,{"derivedFrom":subQ9}),1.0]])]});}
            var Q16;
            {var subQ3=makeQuery(id+"F104.opShell","OFFSET_FACE",FACE,{"disambiguationData":[OSD([sQuery(id+"F0.wireOp",EDGE,"E0.bottom"),sQuery(id+"F0.wireOp",EDGE,"E0.top"),sQuery(id+"F0.wireOp",EDGE,"E0.left"),sQuery(id+"F0.wireOp",EDGE,"E0.right")])]});var subQ4=makeQuery(id+"F116.opExtrude","SWEPT_FACE",FACE,{"disambiguationData":[OSD([sQuery(id+"F115.wireOp",EDGE,"E78")])]});var subQ10=makeQuery(id+"F116.boolean.opBoolean","INTERSECT",EDGE,{"derivedFrom":[subQ3,subQ4]});Q16=makeQuery(id+"F125.imprint","IMPRINT",FACE,{"disambiguationData":[TD([[makeQuery(id+"F125.imprint","IMPRINT",EDGE,{"derivedFrom":subQ10}),1.0]])]});}
            var Q17;
            {var subQ5=makeQuery(id+"F104.opShell","OFFSET_FACE",FACE,{"disambiguationData":[OSD([sQuery(id+"F0.wireOp",EDGE,"E0.bottom"),sQuery(id+"F0.wireOp",EDGE,"E0.top"),sQuery(id+"F0.wireOp",EDGE,"E0.left"),sQuery(id+"F0.wireOp",EDGE,"E0.right")])]});var subQ6=makeQuery(id+"F116.opExtrude","SWEPT_FACE",FACE,{"disambiguationData":[OSD([sQuery(id+"F115.wireOp",EDGE,"E80")])]});var subQ9=makeQuery(id+"F116.boolean.opBoolean","INTERSECT",EDGE,{"derivedFrom":[subQ5,subQ6]});Q17=makeQuery(id+"F125.imprint","IMPRINT",FACE,{"disambiguationData":[TD([[makeQuery(id+"F125.imprint","IMPRINT",EDGE,{"derivedFrom":subQ9}),1.0]])]});}
            var Q18;
            {var subQ5=makeQuery(id+"F104.opShell","OFFSET_FACE",FACE,{"disambiguationData":[OSD([sQuery(id+"F0.wireOp",EDGE,"E0.bottom"),sQuery(id+"F0.wireOp",EDGE,"E0.top"),sQuery(id+"F0.wireOp",EDGE,"E0.left"),sQuery(id+"F0.wireOp",EDGE,"E0.right")])]});var subQ6=makeQuery(id+"F120.opExtrude","SWEPT_FACE",FACE,{"disambiguationData":[OSD([sQuery(id+"F119.wireOp",EDGE,"E85")])]});var subQ9=makeQuery(id+"F120.boolean.opBoolean","INTERSECT",EDGE,{"derivedFrom":[subQ5,subQ6]});Q18=makeQuery(id+"F125.imprint","IMPRINT",FACE,{"disambiguationData":[TD([[makeQuery(id+"F125.imprint","IMPRINT",EDGE,{"derivedFrom":subQ9}),1.0]])]});}
            var Q19;
            {var subQ3=makeQuery(id+"F104.opShell","OFFSET_FACE",FACE,{"disambiguationData":[OSD([sQuery(id+"F0.wireOp",EDGE,"E0.bottom"),sQuery(id+"F0.wireOp",EDGE,"E0.top"),sQuery(id+"F0.wireOp",EDGE,"E0.left"),sQuery(id+"F0.wireOp",EDGE,"E0.right")])]});var subQ4=makeQuery(id+"F120.opExtrude","SWEPT_FACE",FACE,{"disambiguationData":[OSD([sQuery(id+"F119.wireOp",EDGE,"E84")])]});var subQ10=makeQuery(id+"F120.boolean.opBoolean","INTERSECT",EDGE,{"derivedFrom":[subQ3,subQ4]});Q19=makeQuery(id+"F125.imprint","IMPRINT",FACE,{"disambiguationData":[TD([[makeQuery(id+"F125.imprint","IMPRINT",EDGE,{"derivedFrom":subQ10}),1.0]])]});}
            var Q20;
            {var subQ5=makeQuery(id+"F104.opShell","OFFSET_FACE",FACE,{"disambiguationData":[OSD([sQuery(id+"F0.wireOp",EDGE,"E0.bottom"),sQuery(id+"F0.wireOp",EDGE,"E0.top"),sQuery(id+"F0.wireOp",EDGE,"E0.left"),sQuery(id+"F0.wireOp",EDGE,"E0.right")])]});var subQ6=makeQuery(id+"F120.opExtrude","SWEPT_FACE",FACE,{"disambiguationData":[OSD([sQuery(id+"F119.wireOp",EDGE,"E86")])]});var subQ9=makeQuery(id+"F120.boolean.opBoolean","INTERSECT",EDGE,{"derivedFrom":[subQ5,subQ6]});Q20=makeQuery(id+"F125.imprint","IMPRINT",FACE,{"disambiguationData":[TD([[makeQuery(id+"F125.imprint","IMPRINT",EDGE,{"derivedFrom":subQ9}),1.0]])]});}
            var Q21;
            {var subQ5=makeQuery(id+"F104.opShell","OFFSET_FACE",FACE,{"disambiguationData":[OSD([sQuery(id+"F0.wireOp",EDGE,"E0.bottom"),sQuery(id+"F0.wireOp",EDGE,"E0.top"),sQuery(id+"F0.wireOp",EDGE,"E0.left"),sQuery(id+"F0.wireOp",EDGE,"E0.right")])]});var subQ6=makeQuery(id+"F118.opExtrude","SWEPT_FACE",FACE,{"disambiguationData":[OSD([sQuery(id+"F117.wireOp",EDGE,"E82")])]});var subQ9=makeQuery(id+"F118.boolean.opBoolean","INTERSECT",EDGE,{"derivedFrom":[subQ5,subQ6]});Q21=makeQuery(id+"F125.imprint","IMPRINT",FACE,{"disambiguationData":[TD([[makeQuery(id+"F125.imprint","IMPRINT",EDGE,{"derivedFrom":subQ9}),1.0]])]});}
            var Q22;
            {var subQ3=makeQuery(id+"F104.opShell","OFFSET_FACE",FACE,{"disambiguationData":[OSD([sQuery(id+"F0.wireOp",EDGE,"E0.bottom"),sQuery(id+"F0.wireOp",EDGE,"E0.top"),sQuery(id+"F0.wireOp",EDGE,"E0.left"),sQuery(id+"F0.wireOp",EDGE,"E0.right")])]});var subQ4=makeQuery(id+"F118.opExtrude","SWEPT_FACE",FACE,{"disambiguationData":[OSD([sQuery(id+"F117.wireOp",EDGE,"E81")])]});var subQ10=makeQuery(id+"F118.boolean.opBoolean","INTERSECT",EDGE,{"derivedFrom":[subQ3,subQ4]});Q22=makeQuery(id+"F125.imprint","IMPRINT",FACE,{"disambiguationData":[TD([[makeQuery(id+"F125.imprint","IMPRINT",EDGE,{"derivedFrom":subQ10}),1.0]])]});}
            var Q23;
            {var subQ5=makeQuery(id+"F104.opShell","OFFSET_FACE",FACE,{"disambiguationData":[OSD([sQuery(id+"F0.wireOp",EDGE,"E0.bottom"),sQuery(id+"F0.wireOp",EDGE,"E0.top"),sQuery(id+"F0.wireOp",EDGE,"E0.left"),sQuery(id+"F0.wireOp",EDGE,"E0.right")])]});var subQ6=makeQuery(id+"F118.opExtrude","SWEPT_FACE",FACE,{"disambiguationData":[OSD([sQuery(id+"F117.wireOp",EDGE,"E83")])]});var subQ9=makeQuery(id+"F118.boolean.opBoolean","INTERSECT",EDGE,{"derivedFrom":[subQ5,subQ6]});Q23=makeQuery(id+"F125.imprint","IMPRINT",FACE,{"disambiguationData":[TD([[makeQuery(id+"F125.imprint","IMPRINT",EDGE,{"derivedFrom":subQ9}),1.0]])]});}
            var Q24;
            {var subQ5=makeQuery(id+"F104.opShell","OFFSET_FACE",FACE,{"disambiguationData":[OSD([sQuery(id+"F0.wireOp",EDGE,"E0.bottom"),sQuery(id+"F0.wireOp",EDGE,"E0.top"),sQuery(id+"F0.wireOp",EDGE,"E0.left"),sQuery(id+"F0.wireOp",EDGE,"E0.right")])]});var subQ6=makeQuery(id+"F122.opExtrude","SWEPT_FACE",FACE,{"disambiguationData":[OSD([sQuery(id+"F121.wireOp",EDGE,"E88")])]});var subQ9=makeQuery(id+"F122.boolean.opBoolean","INTERSECT",EDGE,{"derivedFrom":[subQ5,subQ6]});Q24=makeQuery(id+"F125.imprint","IMPRINT",FACE,{"disambiguationData":[TD([[makeQuery(id+"F125.imprint","IMPRINT",EDGE,{"derivedFrom":subQ9}),1.0]])]});}
            var Q25;
            {var subQ3=makeQuery(id+"F104.opShell","OFFSET_FACE",FACE,{"disambiguationData":[OSD([sQuery(id+"F0.wireOp",EDGE,"E0.bottom"),sQuery(id+"F0.wireOp",EDGE,"E0.top"),sQuery(id+"F0.wireOp",EDGE,"E0.left"),sQuery(id+"F0.wireOp",EDGE,"E0.right")])]});var subQ4=makeQuery(id+"F122.opExtrude","SWEPT_FACE",FACE,{"disambiguationData":[OSD([sQuery(id+"F121.wireOp",EDGE,"E87")])]});var subQ10=makeQuery(id+"F122.boolean.opBoolean","INTERSECT",EDGE,{"derivedFrom":[subQ3,subQ4]});Q25=makeQuery(id+"F125.imprint","IMPRINT",FACE,{"disambiguationData":[TD([[makeQuery(id+"F125.imprint","IMPRINT",EDGE,{"derivedFrom":subQ10}),-1.0]])]});}
            var Q26;
            {var subQ3=makeQuery(id+"F104.opShell","OFFSET_FACE",FACE,{"disambiguationData":[OSD([sQuery(id+"F0.wireOp",EDGE,"E0.bottom"),sQuery(id+"F0.wireOp",EDGE,"E0.top"),sQuery(id+"F0.wireOp",EDGE,"E0.left"),sQuery(id+"F0.wireOp",EDGE,"E0.right")])]});var subQ4=makeQuery(id+"F122.opExtrude","SWEPT_FACE",FACE,{"disambiguationData":[OSD([sQuery(id+"F121.wireOp",EDGE,"E87")])]});var subQ10=makeQuery(id+"F122.boolean.opBoolean","INTERSECT",EDGE,{"derivedFrom":[subQ3,subQ4]});Q26=makeQuery(id+"F125.imprint","IMPRINT",FACE,{"disambiguationData":[TD([[makeQuery(id+"F125.imprint","IMPRINT",EDGE,{"derivedFrom":subQ10}),1.0]])]});}
            var Q27;
            {var subQ5=makeQuery(id+"F104.opShell","OFFSET_FACE",FACE,{"disambiguationData":[OSD([sQuery(id+"F0.wireOp",EDGE,"E0.bottom"),sQuery(id+"F0.wireOp",EDGE,"E0.top"),sQuery(id+"F0.wireOp",EDGE,"E0.left"),sQuery(id+"F0.wireOp",EDGE,"E0.right")])]});var subQ6=makeQuery(id+"F122.opExtrude","SWEPT_FACE",FACE,{"disambiguationData":[OSD([sQuery(id+"F121.wireOp",EDGE,"E89")])]});var subQ9=makeQuery(id+"F122.boolean.opBoolean","INTERSECT",EDGE,{"derivedFrom":[subQ5,subQ6]});Q27=makeQuery(id+"F125.imprint","IMPRINT",FACE,{"disambiguationData":[TD([[makeQuery(id+"F125.imprint","IMPRINT",EDGE,{"derivedFrom":subQ9}),1.0]])]});}
            var Q28;
            {var subQ5=makeQuery(id+"F104.opShell","OFFSET_FACE",FACE,{"disambiguationData":[OSD([sQuery(id+"F0.wireOp",EDGE,"E0.bottom"),sQuery(id+"F0.wireOp",EDGE,"E0.top"),sQuery(id+"F0.wireOp",EDGE,"E0.left"),sQuery(id+"F0.wireOp",EDGE,"E0.right")])]});var subQ6=makeQuery(id+"F124.opExtrude","SWEPT_FACE",FACE,{"disambiguationData":[OSD([sQuery(id+"F123.wireOp",EDGE,"E91")])]});var subQ9=makeQuery(id+"F124.boolean.opBoolean","INTERSECT",EDGE,{"derivedFrom":[subQ5,subQ6]});Q28=makeQuery(id+"F125.imprint","IMPRINT",FACE,{"disambiguationData":[TD([[makeQuery(id+"F125.imprint","IMPRINT",EDGE,{"derivedFrom":subQ9}),1.0]])]});}
            var Q29;
            {var subQ3=makeQuery(id+"F104.opShell","OFFSET_FACE",FACE,{"disambiguationData":[OSD([sQuery(id+"F0.wireOp",EDGE,"E0.bottom"),sQuery(id+"F0.wireOp",EDGE,"E0.top"),sQuery(id+"F0.wireOp",EDGE,"E0.left"),sQuery(id+"F0.wireOp",EDGE,"E0.right")])]});var subQ4=makeQuery(id+"F124.opExtrude","SWEPT_FACE",FACE,{"disambiguationData":[OSD([sQuery(id+"F123.wireOp",EDGE,"E90")])]});var subQ10=makeQuery(id+"F124.boolean.opBoolean","INTERSECT",EDGE,{"derivedFrom":[subQ3,subQ4]});Q29=makeQuery(id+"F125.imprint","IMPRINT",FACE,{"disambiguationData":[TD([[makeQuery(id+"F125.imprint","IMPRINT",EDGE,{"derivedFrom":subQ10}),1.0]])]});}
            var Q30;
            {var subQ5=makeQuery(id+"F104.opShell","OFFSET_FACE",FACE,{"disambiguationData":[OSD([sQuery(id+"F0.wireOp",EDGE,"E0.bottom"),sQuery(id+"F0.wireOp",EDGE,"E0.top"),sQuery(id+"F0.wireOp",EDGE,"E0.left"),sQuery(id+"F0.wireOp",EDGE,"E0.right")])]});var subQ6=makeQuery(id+"F124.opExtrude","SWEPT_FACE",FACE,{"disambiguationData":[OSD([sQuery(id+"F123.wireOp",EDGE,"E92")])]});var subQ9=makeQuery(id+"F124.boolean.opBoolean","INTERSECT",EDGE,{"derivedFrom":[subQ5,subQ6]});Q30=makeQuery(id+"F125.imprint","IMPRINT",FACE,{"disambiguationData":[TD([[makeQuery(id+"F125.imprint","IMPRINT",EDGE,{"derivedFrom":subQ9}),1.0]])]});}
            extrude(context, id + "F126", {"entities" : qUnion([Q0, Q1, Q2, Q3, Q4, Q5, Q6, Q7, Q8, Q9, Q10, Q11, Q12, Q13, Q14, Q15, Q16, Q17, Q18, Q19, Q20, Q21, Q22, Q23, Q24, Q25, Q26, Q27, Q28, Q29, Q30]), "operationType" : NewBodyOperationType.REMOVE, "oppositeDirection" : true, "depth" : 3.17 * mm, "offsetDistance" : 25.4 * mm});
        }
    });
